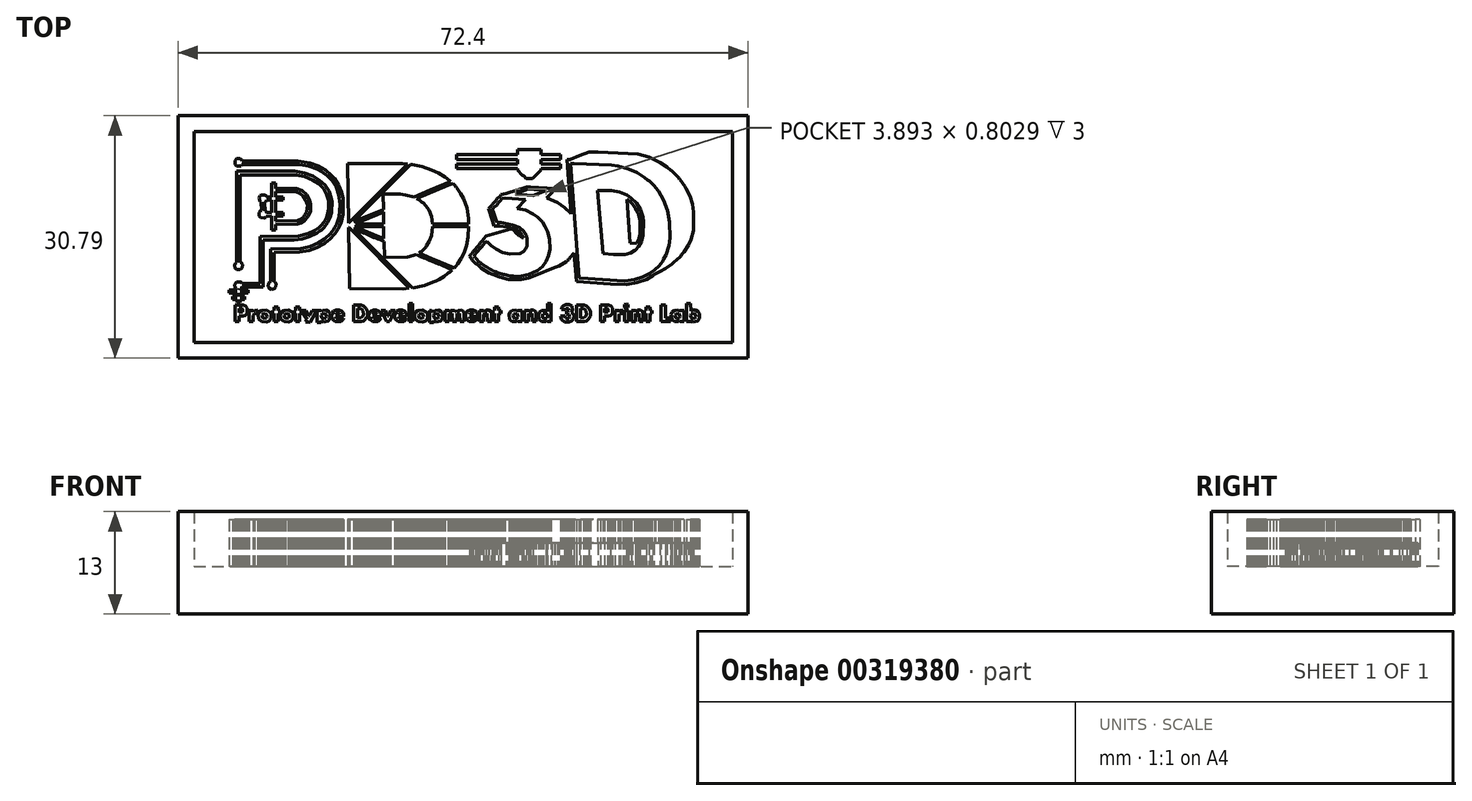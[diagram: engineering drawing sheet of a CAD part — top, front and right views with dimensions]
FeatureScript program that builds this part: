
annotation { "Feature Type Name" : "Feature", "Feature Type Description" : "" }
export const myFeature = defineFeature(function(context is Context, id is Id, definition is map)
    precondition{}
    {
        {
            var Q0;
            Q0=qCreatedBy(makeId("Top.planeOp"),FACE);
            var sketch = newSketch(context, id + "F0", { "sketchPlane" : qUnion([Q0])});
            skLineSegment(sketch, "E0", {"start": v(0.17, -1.62) * mm, "end": v(0.12, -1.63) * mm});
            skLineSegment(sketch, "E1", {"start": v(0.12, -1.63) * mm, "end": v(0.1, -1.66) * mm});
            skLineSegment(sketch, "E2", {"start": v(0.1, -1.66) * mm, "end": v(0.2, -1.65) * mm});
            skLineSegment(sketch, "E3", {"start": v(0.2, -1.65) * mm, "end": v(0.19, -1.63) * mm});
            skLineSegment(sketch, "E4", {"start": v(0.19, -1.63) * mm, "end": v(0.17, -1.62) * mm});
            skLineSegment(sketch, "E5", {"start": v(-1.33, -1.62) * mm, "end": v(-1.38, -1.63) * mm});
            skLineSegment(sketch, "E6", {"start": v(-1.38, -1.63) * mm, "end": v(-1.4, -1.66) * mm});
            skLineSegment(sketch, "E7", {"start": v(-1.4, -1.66) * mm, "end": v(-1.3, -1.65) * mm});
            skLineSegment(sketch, "E8", {"start": v(-1.3, -1.65) * mm, "end": v(-1.31, -1.63) * mm});
            skLineSegment(sketch, "E9", {"start": v(-1.31, -1.63) * mm, "end": v(-1.33, -1.62) * mm});
            skLineSegment(sketch, "E10", {"start": v(-1.87, -1.62) * mm, "end": v(-1.92, -1.63) * mm});
            skLineSegment(sketch, "E11", {"start": v(-1.92, -1.63) * mm, "end": v(-1.94, -1.66) * mm});
            skLineSegment(sketch, "E12", {"start": v(-1.94, -1.66) * mm, "end": v(-1.85, -1.65) * mm});
            skLineSegment(sketch, "E13", {"start": v(-1.85, -1.65) * mm, "end": v(-1.86, -1.63) * mm});
            skLineSegment(sketch, "E14", {"start": v(-1.86, -1.63) * mm, "end": v(-1.87, -1.62) * mm});
            skLineSegment(sketch, "E15", {"start": v(-2.66, -1.62) * mm, "end": v(-2.71, -1.63) * mm});
            skLineSegment(sketch, "E16", {"start": v(-2.71, -1.63) * mm, "end": v(-2.73, -1.66) * mm});
            skLineSegment(sketch, "E17", {"start": v(-2.73, -1.66) * mm, "end": v(-2.64, -1.65) * mm});
            skLineSegment(sketch, "E18", {"start": v(-2.64, -1.65) * mm, "end": v(-2.64, -1.63) * mm});
            skLineSegment(sketch, "E19", {"start": v(-2.64, -1.63) * mm, "end": v(-2.66, -1.62) * mm});
            skLineSegment(sketch, "E20", {"start": v(4.87, -1.64) * mm, "end": v(4.8, -1.65) * mm});
            skLineSegment(sketch, "E21", {"start": v(4.8, -1.65) * mm, "end": v(4.79, -1.67) * mm});
            skLineSegment(sketch, "E22", {"start": v(4.79, -1.67) * mm, "end": v(4.8, -1.72) * mm});
            skLineSegment(sketch, "E23", {"start": v(4.8, -1.72) * mm, "end": v(4.8, -1.72) * mm});
            skLineSegment(sketch, "E24", {"start": v(4.8, -1.72) * mm, "end": v(4.82, -1.74) * mm});
            skLineSegment(sketch, "E25", {"start": v(4.82, -1.74) * mm, "end": v(4.89, -1.73) * mm});
            skLineSegment(sketch, "E26", {"start": v(4.89, -1.73) * mm, "end": v(4.9, -1.7) * mm});
            skLineSegment(sketch, "E27", {"start": v(4.9, -1.7) * mm, "end": v(4.9, -1.66) * mm});
            skLineSegment(sketch, "E28", {"start": v(4.9, -1.66) * mm, "end": v(4.87, -1.64) * mm});
            skLineSegment(sketch, "E29", {"start": v(4.55, -1.64) * mm, "end": v(4.48, -1.65) * mm});
            skLineSegment(sketch, "E30", {"start": v(4.48, -1.65) * mm, "end": v(4.46, -1.67) * mm});
            skLineSegment(sketch, "E31", {"start": v(4.46, -1.67) * mm, "end": v(4.47, -1.72) * mm});
            skLineSegment(sketch, "E32", {"start": v(4.47, -1.72) * mm, "end": v(4.48, -1.72) * mm});
            skLineSegment(sketch, "E33", {"start": v(4.48, -1.72) * mm, "end": v(4.5, -1.74) * mm});
            skLineSegment(sketch, "E34", {"start": v(4.5, -1.74) * mm, "end": v(4.55, -1.73) * mm});
            skLineSegment(sketch, "E35", {"start": v(4.55, -1.73) * mm, "end": v(4.57, -1.72) * mm});
            skLineSegment(sketch, "E36", {"start": v(4.57, -1.72) * mm, "end": v(4.56, -1.66) * mm});
            skLineSegment(sketch, "E37", {"start": v(4.56, -1.66) * mm, "end": v(4.55, -1.64) * mm});
            skLineSegment(sketch, "E38", {"start": v(1.73, -1.64) * mm, "end": v(1.67, -1.65) * mm});
            skLineSegment(sketch, "E39", {"start": v(1.67, -1.65) * mm, "end": v(1.65, -1.67) * mm});
            skLineSegment(sketch, "E40", {"start": v(1.65, -1.67) * mm, "end": v(1.66, -1.72) * mm});
            skLineSegment(sketch, "E41", {"start": v(1.66, -1.72) * mm, "end": v(1.67, -1.72) * mm});
            skLineSegment(sketch, "E42", {"start": v(1.67, -1.72) * mm, "end": v(1.68, -1.74) * mm});
            skLineSegment(sketch, "E43", {"start": v(1.68, -1.74) * mm, "end": v(1.75, -1.73) * mm});
            skLineSegment(sketch, "E44", {"start": v(1.75, -1.73) * mm, "end": v(1.77, -1.7) * mm});
            skLineSegment(sketch, "E45", {"start": v(1.77, -1.7) * mm, "end": v(1.76, -1.66) * mm});
            skLineSegment(sketch, "E46", {"start": v(1.76, -1.66) * mm, "end": v(1.73, -1.64) * mm});
            skLineSegment(sketch, "E47", {"start": v(1.11, -1.64) * mm, "end": v(1.05, -1.65) * mm});
            skLineSegment(sketch, "E48", {"start": v(1.05, -1.65) * mm, "end": v(1.03, -1.67) * mm});
            skLineSegment(sketch, "E49", {"start": v(1.03, -1.67) * mm, "end": v(1.04, -1.72) * mm});
            skLineSegment(sketch, "E50", {"start": v(1.04, -1.72) * mm, "end": v(1.05, -1.72) * mm});
            skLineSegment(sketch, "E51", {"start": v(1.05, -1.72) * mm, "end": v(1.06, -1.74) * mm});
            skLineSegment(sketch, "E52", {"start": v(1.06, -1.74) * mm, "end": v(1.12, -1.73) * mm});
            skLineSegment(sketch, "E53", {"start": v(1.12, -1.73) * mm, "end": v(1.14, -1.72) * mm});
            skLineSegment(sketch, "E54", {"start": v(1.14, -1.72) * mm, "end": v(1.13, -1.66) * mm});
            skLineSegment(sketch, "E55", {"start": v(1.13, -1.66) * mm, "end": v(1.11, -1.64) * mm});
            skLineSegment(sketch, "E56", {"start": v(-0.57, -1.64) * mm, "end": v(-0.64, -1.65) * mm});
            skLineSegment(sketch, "E57", {"start": v(-0.64, -1.65) * mm, "end": v(-0.65, -1.67) * mm});
            skLineSegment(sketch, "E58", {"start": v(-0.65, -1.67) * mm, "end": v(-0.64, -1.72) * mm});
            skLineSegment(sketch, "E59", {"start": v(-0.64, -1.72) * mm, "end": v(-0.64, -1.72) * mm});
            skLineSegment(sketch, "E60", {"start": v(-0.64, -1.72) * mm, "end": v(-0.62, -1.74) * mm});
            skLineSegment(sketch, "E61", {"start": v(-0.62, -1.74) * mm, "end": v(-0.55, -1.73) * mm});
            skLineSegment(sketch, "E62", {"start": v(-0.55, -1.73) * mm, "end": v(-0.54, -1.7) * mm});
            skLineSegment(sketch, "E63", {"start": v(-0.54, -1.7) * mm, "end": v(-0.55, -1.66) * mm});
            skLineSegment(sketch, "E64", {"start": v(-0.55, -1.66) * mm, "end": v(-0.57, -1.64) * mm});
            skLineSegment(sketch, "E65", {"start": v(-2.95, -1.64) * mm, "end": v(-3.02, -1.65) * mm});
            skLineSegment(sketch, "E66", {"start": v(-3.02, -1.65) * mm, "end": v(-3.03, -1.67) * mm});
            skLineSegment(sketch, "E67", {"start": v(-3.03, -1.67) * mm, "end": v(-3.02, -1.72) * mm});
            skLineSegment(sketch, "E68", {"start": v(-3.02, -1.72) * mm, "end": v(-3.02, -1.72) * mm});
            skLineSegment(sketch, "E69", {"start": v(-3.02, -1.72) * mm, "end": v(-3, -1.74) * mm});
            skLineSegment(sketch, "E70", {"start": v(-3, -1.74) * mm, "end": v(-2.93, -1.73) * mm});
            skLineSegment(sketch, "E71", {"start": v(-2.93, -1.73) * mm, "end": v(-2.92, -1.7) * mm});
            skLineSegment(sketch, "E72", {"start": v(-2.92, -1.7) * mm, "end": v(-2.92, -1.66) * mm});
            skLineSegment(sketch, "E73", {"start": v(-2.92, -1.66) * mm, "end": v(-2.95, -1.64) * mm});
            skLineSegment(sketch, "E74", {"start": v(-0.9, -1.64) * mm, "end": v(-0.95, -1.65) * mm});
            skLineSegment(sketch, "E75", {"start": v(-0.95, -1.65) * mm, "end": v(-0.97, -1.67) * mm});
            skLineSegment(sketch, "E76", {"start": v(-0.97, -1.67) * mm, "end": v(-0.96, -1.72) * mm});
            skLineSegment(sketch, "E77", {"start": v(-0.96, -1.72) * mm, "end": v(-0.95, -1.72) * mm});
            skLineSegment(sketch, "E78", {"start": v(-0.95, -1.72) * mm, "end": v(-0.95, -1.74) * mm});
            skLineSegment(sketch, "E79", {"start": v(-0.95, -1.74) * mm, "end": v(-0.88, -1.73) * mm});
            skLineSegment(sketch, "E80", {"start": v(-0.88, -1.73) * mm, "end": v(-0.86, -1.7) * mm});
            skLineSegment(sketch, "E81", {"start": v(-0.86, -1.7) * mm, "end": v(-0.87, -1.66) * mm});
            skLineSegment(sketch, "E82", {"start": v(-0.87, -1.66) * mm, "end": v(-0.9, -1.64) * mm});
            skLineSegment(sketch, "E83", {"start": v(-3.73, -1.64) * mm, "end": v(-3.8, -1.65) * mm});
            skLineSegment(sketch, "E84", {"start": v(-3.8, -1.65) * mm, "end": v(-3.81, -1.67) * mm});
            skLineSegment(sketch, "E85", {"start": v(-3.81, -1.67) * mm, "end": v(-3.8, -1.72) * mm});
            skLineSegment(sketch, "E86", {"start": v(-3.8, -1.72) * mm, "end": v(-3.8, -1.72) * mm});
            skLineSegment(sketch, "E87", {"start": v(-3.8, -1.72) * mm, "end": v(-3.79, -1.74) * mm});
            skLineSegment(sketch, "E88", {"start": v(-3.79, -1.74) * mm, "end": v(-3.72, -1.73) * mm});
            skLineSegment(sketch, "E89", {"start": v(-3.72, -1.73) * mm, "end": v(-3.7, -1.7) * mm});
            skLineSegment(sketch, "E90", {"start": v(-3.7, -1.7) * mm, "end": v(-3.71, -1.66) * mm});
            skLineSegment(sketch, "E91", {"start": v(-3.71, -1.66) * mm, "end": v(-3.73, -1.64) * mm});
            skLineSegment(sketch, "E92", {"start": v(-4.2, -1.64) * mm, "end": v(-4.27, -1.65) * mm});
            skLineSegment(sketch, "E93", {"start": v(-4.27, -1.65) * mm, "end": v(-4.28, -1.67) * mm});
            skLineSegment(sketch, "E94", {"start": v(-4.28, -1.67) * mm, "end": v(-4.27, -1.72) * mm});
            skLineSegment(sketch, "E95", {"start": v(-4.27, -1.72) * mm, "end": v(-4.27, -1.72) * mm});
            skLineSegment(sketch, "E96", {"start": v(-4.27, -1.72) * mm, "end": v(-4.26, -1.74) * mm});
            skLineSegment(sketch, "E97", {"start": v(-4.26, -1.74) * mm, "end": v(-4.19, -1.73) * mm});
            skLineSegment(sketch, "E98", {"start": v(-4.19, -1.73) * mm, "end": v(-4.17, -1.7) * mm});
            skLineSegment(sketch, "E99", {"start": v(-4.17, -1.7) * mm, "end": v(-4.18, -1.66) * mm});
            skLineSegment(sketch, "E100", {"start": v(-4.18, -1.66) * mm, "end": v(-4.2, -1.64) * mm});
            skLineSegment(sketch, "E101", {"start": v(3.45, -1.44) * mm, "end": v(3.47, -1.45) * mm});
            skLineSegment(sketch, "E102", {"start": v(3.47, -1.45) * mm, "end": v(3.47, -1.51) * mm});
            skLineSegment(sketch, "E103", {"start": v(3.47, -1.51) * mm, "end": v(3.42, -1.53) * mm});
            skLineSegment(sketch, "E104", {"start": v(3.42, -1.53) * mm, "end": v(3.4, -1.51) * mm});
            skLineSegment(sketch, "E105", {"start": v(3.4, -1.51) * mm, "end": v(3.4, -1.45) * mm});
            skLineSegment(sketch, "E106", {"start": v(3.4, -1.45) * mm, "end": v(3.45, -1.44) * mm});
            skLineSegment(sketch, "E107", {"start": v(2.21, -1.44) * mm, "end": v(2.28, -1.48) * mm});
            skLineSegment(sketch, "E108", {"start": v(2.28, -1.48) * mm, "end": v(2.3, -1.56) * mm});
            skLineSegment(sketch, "E109", {"start": v(2.3, -1.56) * mm, "end": v(2.27, -1.6) * mm});
            skLineSegment(sketch, "E110", {"start": v(2.27, -1.6) * mm, "end": v(2.26, -1.62) * mm});
            skLineSegment(sketch, "E111", {"start": v(2.26, -1.62) * mm, "end": v(2.28, -1.62) * mm});
            skLineSegment(sketch, "E112", {"start": v(2.28, -1.62) * mm, "end": v(2.32, -1.68) * mm});
            skLineSegment(sketch, "E113", {"start": v(2.32, -1.68) * mm, "end": v(2.31, -1.75) * mm});
            skLineSegment(sketch, "E114", {"start": v(2.31, -1.75) * mm, "end": v(2.27, -1.8) * mm});
            skLineSegment(sketch, "E115", {"start": v(2.27, -1.8) * mm, "end": v(2.21, -1.82) * mm});
            skLineSegment(sketch, "E116", {"start": v(2.21, -1.82) * mm, "end": v(2.12, -1.81) * mm});
            skLineSegment(sketch, "E117", {"start": v(2.12, -1.81) * mm, "end": v(2.06, -1.77) * mm});
            skLineSegment(sketch, "E118", {"start": v(2.06, -1.77) * mm, "end": v(2.04, -1.7) * mm});
            skLineSegment(sketch, "E119", {"start": v(2.04, -1.7) * mm, "end": v(2.13, -1.7) * mm});
            skLineSegment(sketch, "E120", {"start": v(2.13, -1.7) * mm, "end": v(2.14, -1.73) * mm});
            skLineSegment(sketch, "E121", {"start": v(2.14, -1.73) * mm, "end": v(2.15, -1.73) * mm});
            skLineSegment(sketch, "E122", {"start": v(2.15, -1.73) * mm, "end": v(2.16, -1.75) * mm});
            skLineSegment(sketch, "E123", {"start": v(2.16, -1.75) * mm, "end": v(2.21, -1.74) * mm});
            skLineSegment(sketch, "E124", {"start": v(2.21, -1.74) * mm, "end": v(2.23, -1.72) * mm});
            skLineSegment(sketch, "E125", {"start": v(2.23, -1.72) * mm, "end": v(2.22, -1.66) * mm});
            skLineSegment(sketch, "E126", {"start": v(2.22, -1.66) * mm, "end": v(2.17, -1.65) * mm});
            skLineSegment(sketch, "E127", {"start": v(2.17, -1.65) * mm, "end": v(2.17, -1.59) * mm});
            skLineSegment(sketch, "E128", {"start": v(2.17, -1.59) * mm, "end": v(2.21, -1.57) * mm});
            skLineSegment(sketch, "E129", {"start": v(2.21, -1.57) * mm, "end": v(2.2, -1.53) * mm});
            skLineSegment(sketch, "E130", {"start": v(2.2, -1.53) * mm, "end": v(2.15, -1.53) * mm});
            skLineSegment(sketch, "E131", {"start": v(2.15, -1.53) * mm, "end": v(2.14, -1.56) * mm});
            skLineSegment(sketch, "E132", {"start": v(2.14, -1.56) * mm, "end": v(2.06, -1.55) * mm});
            skLineSegment(sketch, "E133", {"start": v(2.06, -1.55) * mm, "end": v(2.07, -1.5) * mm});
            skLineSegment(sketch, "E134", {"start": v(2.07, -1.5) * mm, "end": v(2.1, -1.47) * mm});
            skLineSegment(sketch, "E135", {"start": v(2.1, -1.47) * mm, "end": v(2.15, -1.44) * mm});
            skLineSegment(sketch, "E136", {"start": v(2.15, -1.44) * mm, "end": v(2.21, -1.44) * mm});
            skLineSegment(sketch, "E137", {"start": v(3.05, -1.46) * mm, "end": v(3.1, -1.48) * mm});
            skLineSegment(sketch, "E138", {"start": v(3.1, -1.48) * mm, "end": v(3.14, -1.52) * mm});
            skLineSegment(sketch, "E139", {"start": v(3.14, -1.52) * mm, "end": v(3.14, -1.63) * mm});
            skLineSegment(sketch, "E140", {"start": v(3.14, -1.63) * mm, "end": v(3.1, -1.68) * mm});
            skLineSegment(sketch, "E141", {"start": v(3.1, -1.68) * mm, "end": v(3.05, -1.7) * mm});
            skLineSegment(sketch, "E142", {"start": v(3.05, -1.7) * mm, "end": v(2.97, -1.7) * mm});
            skLineSegment(sketch, "E143", {"start": v(2.97, -1.7) * mm, "end": v(2.97, -1.8) * mm});
            skLineSegment(sketch, "E144", {"start": v(2.97, -1.8) * mm, "end": v(2.88, -1.8) * mm});
            skLineSegment(sketch, "E145", {"start": v(2.88, -1.8) * mm, "end": v(2.88, -1.46) * mm});
            skLineSegment(sketch, "E146", {"start": v(2.88, -1.46) * mm, "end": v(3.05, -1.46) * mm});
            skLineSegment(sketch, "E147", {"start": v(2.54, -1.46) * mm, "end": v(2.6, -1.48) * mm});
            skLineSegment(sketch, "E148", {"start": v(2.6, -1.48) * mm, "end": v(2.64, -1.53) * mm});
            skLineSegment(sketch, "E149", {"start": v(2.64, -1.53) * mm, "end": v(2.67, -1.6) * mm});
            skLineSegment(sketch, "E150", {"start": v(2.67, -1.6) * mm, "end": v(2.67, -1.7) * mm});
            skLineSegment(sketch, "E151", {"start": v(2.67, -1.7) * mm, "end": v(2.63, -1.75) * mm});
            skLineSegment(sketch, "E152", {"start": v(2.63, -1.75) * mm, "end": v(2.58, -1.8) * mm});
            skLineSegment(sketch, "E153", {"start": v(2.58, -1.8) * mm, "end": v(2.54, -1.8) * mm});
            skLineSegment(sketch, "E154", {"start": v(2.54, -1.8) * mm, "end": v(2.37, -1.8) * mm});
            skLineSegment(sketch, "E155", {"start": v(2.37, -1.8) * mm, "end": v(2.37, -1.46) * mm});
            skLineSegment(sketch, "E156", {"start": v(2.37, -1.46) * mm, "end": v(2.54, -1.46) * mm});
            skLineSegment(sketch, "E157", {"start": v(-2.18, -1.46) * mm, "end": v(-2.13, -1.48) * mm});
            skLineSegment(sketch, "E158", {"start": v(-2.13, -1.48) * mm, "end": v(-2.08, -1.53) * mm});
            skLineSegment(sketch, "E159", {"start": v(-2.08, -1.53) * mm, "end": v(-2.05, -1.6) * mm});
            skLineSegment(sketch, "E160", {"start": v(-2.05, -1.6) * mm, "end": v(-2.05, -1.7) * mm});
            skLineSegment(sketch, "E161", {"start": v(-2.05, -1.7) * mm, "end": v(-2.1, -1.76) * mm});
            skLineSegment(sketch, "E162", {"start": v(-2.1, -1.76) * mm, "end": v(-2.14, -1.8) * mm});
            skLineSegment(sketch, "E163", {"start": v(-2.14, -1.8) * mm, "end": v(-2.18, -1.8) * mm});
            skLineSegment(sketch, "E164", {"start": v(-2.18, -1.8) * mm, "end": v(-2.35, -1.8) * mm});
            skLineSegment(sketch, "E165", {"start": v(-2.35, -1.8) * mm, "end": v(-2.35, -1.46) * mm});
            skLineSegment(sketch, "E166", {"start": v(-2.35, -1.46) * mm, "end": v(-2.18, -1.46) * mm});
            skLineSegment(sketch, "E167", {"start": v(-4.68, -1.46) * mm, "end": v(-4.63, -1.48) * mm});
            skLineSegment(sketch, "E168", {"start": v(-4.63, -1.48) * mm, "end": v(-4.6, -1.52) * mm});
            skLineSegment(sketch, "E169", {"start": v(-4.6, -1.52) * mm, "end": v(-4.6, -1.63) * mm});
            skLineSegment(sketch, "E170", {"start": v(-4.6, -1.63) * mm, "end": v(-4.64, -1.68) * mm});
            skLineSegment(sketch, "E171", {"start": v(-4.64, -1.68) * mm, "end": v(-4.68, -1.7) * mm});
            skLineSegment(sketch, "E172", {"start": v(-4.68, -1.7) * mm, "end": v(-4.77, -1.7) * mm});
            skLineSegment(sketch, "E173", {"start": v(-4.77, -1.7) * mm, "end": v(-4.77, -1.8) * mm});
            skLineSegment(sketch, "E174", {"start": v(-4.77, -1.8) * mm, "end": v(-4.86, -1.8) * mm});
            skLineSegment(sketch, "E175", {"start": v(-4.86, -1.8) * mm, "end": v(-4.86, -1.46) * mm});
            skLineSegment(sketch, "E176", {"start": v(-4.86, -1.46) * mm, "end": v(-4.68, -1.46) * mm});
            skLineSegment(sketch, "E177", {"start": v(4.52, -1.56) * mm, "end": v(4.57, -1.6) * mm});
            skLineSegment(sketch, "E178", {"start": v(4.57, -1.6) * mm, "end": v(4.57, -1.57) * mm});
            skLineSegment(sketch, "E179", {"start": v(4.57, -1.57) * mm, "end": v(4.65, -1.57) * mm});
            skLineSegment(sketch, "E180", {"start": v(4.65, -1.57) * mm, "end": v(4.65, -1.8) * mm});
            skLineSegment(sketch, "E181", {"start": v(4.65, -1.8) * mm, "end": v(4.57, -1.8) * mm});
            skLineSegment(sketch, "E182", {"start": v(4.57, -1.8) * mm, "end": v(4.56, -1.78) * mm});
            skLineSegment(sketch, "E183", {"start": v(4.56, -1.78) * mm, "end": v(4.54, -1.8) * mm});
            skLineSegment(sketch, "E184", {"start": v(4.54, -1.8) * mm, "end": v(4.45, -1.8) * mm});
            skLineSegment(sketch, "E185", {"start": v(4.45, -1.8) * mm, "end": v(4.4, -1.76) * mm});
            skLineSegment(sketch, "E186", {"start": v(4.4, -1.76) * mm, "end": v(4.38, -1.66) * mm});
            skLineSegment(sketch, "E187", {"start": v(4.38, -1.66) * mm, "end": v(4.4, -1.6) * mm});
            skLineSegment(sketch, "E188", {"start": v(4.4, -1.6) * mm, "end": v(4.45, -1.57) * mm});
            skLineSegment(sketch, "E189", {"start": v(4.45, -1.57) * mm, "end": v(4.52, -1.56) * mm});
            skLineSegment(sketch, "E190", {"start": v(3.93, -1.5) * mm, "end": v(3.93, -1.57) * mm});
            skLineSegment(sketch, "E191", {"start": v(3.93, -1.57) * mm, "end": v(3.98, -1.57) * mm});
            skLineSegment(sketch, "E192", {"start": v(3.98, -1.57) * mm, "end": v(3.98, -1.64) * mm});
            skLineSegment(sketch, "E193", {"start": v(3.98, -1.64) * mm, "end": v(3.93, -1.64) * mm});
            skLineSegment(sketch, "E194", {"start": v(3.93, -1.64) * mm, "end": v(3.93, -1.8) * mm});
            skLineSegment(sketch, "E195", {"start": v(3.93, -1.8) * mm, "end": v(3.85, -1.8) * mm});
            skLineSegment(sketch, "E196", {"start": v(3.85, -1.8) * mm, "end": v(3.85, -1.64) * mm});
            skLineSegment(sketch, "E197", {"start": v(3.85, -1.64) * mm, "end": v(3.82, -1.64) * mm});
            skLineSegment(sketch, "E198", {"start": v(3.82, -1.64) * mm, "end": v(3.82, -1.57) * mm});
            skLineSegment(sketch, "E199", {"start": v(3.82, -1.57) * mm, "end": v(3.85, -1.57) * mm});
            skLineSegment(sketch, "E200", {"start": v(3.85, -1.57) * mm, "end": v(3.85, -1.5) * mm});
            skLineSegment(sketch, "E201", {"start": v(3.85, -1.5) * mm, "end": v(3.93, -1.5) * mm});
            skLineSegment(sketch, "E202", {"start": v(3.73, -1.56) * mm, "end": v(3.77, -1.6) * mm});
            skLineSegment(sketch, "E203", {"start": v(3.77, -1.6) * mm, "end": v(3.79, -1.63) * mm});
            skLineSegment(sketch, "E204", {"start": v(3.79, -1.63) * mm, "end": v(3.79, -1.8) * mm});
            skLineSegment(sketch, "E205", {"start": v(3.79, -1.8) * mm, "end": v(3.7, -1.8) * mm});
            skLineSegment(sketch, "E206", {"start": v(3.7, -1.8) * mm, "end": v(3.7, -1.64) * mm});
            skLineSegment(sketch, "E207", {"start": v(3.7, -1.64) * mm, "end": v(3.64, -1.64) * mm});
            skLineSegment(sketch, "E208", {"start": v(3.64, -1.64) * mm, "end": v(3.62, -1.66) * mm});
            skLineSegment(sketch, "E209", {"start": v(3.62, -1.66) * mm, "end": v(3.62, -1.8) * mm});
            skLineSegment(sketch, "E210", {"start": v(3.62, -1.8) * mm, "end": v(3.54, -1.8) * mm});
            skLineSegment(sketch, "E211", {"start": v(3.54, -1.8) * mm, "end": v(3.54, -1.57) * mm});
            skLineSegment(sketch, "E212", {"start": v(3.54, -1.57) * mm, "end": v(3.62, -1.57) * mm});
            skLineSegment(sketch, "E213", {"start": v(3.62, -1.57) * mm, "end": v(3.63, -1.6) * mm});
            skLineSegment(sketch, "E214", {"start": v(3.63, -1.6) * mm, "end": v(3.64, -1.58) * mm});
            skLineSegment(sketch, "E215", {"start": v(3.64, -1.58) * mm, "end": v(3.67, -1.56) * mm});
            skLineSegment(sketch, "E216", {"start": v(3.67, -1.56) * mm, "end": v(3.73, -1.56) * mm});
            skLineSegment(sketch, "E217", {"start": v(1.46, -1.56) * mm, "end": v(1.5, -1.6) * mm});
            skLineSegment(sketch, "E218", {"start": v(1.5, -1.6) * mm, "end": v(1.52, -1.63) * mm});
            skLineSegment(sketch, "E219", {"start": v(1.52, -1.63) * mm, "end": v(1.52, -1.8) * mm});
            skLineSegment(sketch, "E220", {"start": v(1.52, -1.8) * mm, "end": v(1.44, -1.8) * mm});
            skLineSegment(sketch, "E221", {"start": v(1.44, -1.8) * mm, "end": v(1.43, -1.64) * mm});
            skLineSegment(sketch, "E222", {"start": v(1.43, -1.64) * mm, "end": v(1.37, -1.64) * mm});
            skLineSegment(sketch, "E223", {"start": v(1.37, -1.64) * mm, "end": v(1.36, -1.66) * mm});
            skLineSegment(sketch, "E224", {"start": v(1.36, -1.66) * mm, "end": v(1.36, -1.8) * mm});
            skLineSegment(sketch, "E225", {"start": v(1.36, -1.8) * mm, "end": v(1.27, -1.8) * mm});
            skLineSegment(sketch, "E226", {"start": v(1.27, -1.8) * mm, "end": v(1.27, -1.57) * mm});
            skLineSegment(sketch, "E227", {"start": v(1.27, -1.57) * mm, "end": v(1.36, -1.57) * mm});
            skLineSegment(sketch, "E228", {"start": v(1.36, -1.57) * mm, "end": v(1.36, -1.6) * mm});
            skLineSegment(sketch, "E229", {"start": v(1.36, -1.6) * mm, "end": v(1.37, -1.58) * mm});
            skLineSegment(sketch, "E230", {"start": v(1.37, -1.58) * mm, "end": v(1.4, -1.56) * mm});
            skLineSegment(sketch, "E231", {"start": v(1.4, -1.56) * mm, "end": v(1.46, -1.56) * mm});
            skLineSegment(sketch, "E232", {"start": v(1.1, -1.56) * mm, "end": v(1.14, -1.6) * mm});
            skLineSegment(sketch, "E233", {"start": v(1.14, -1.6) * mm, "end": v(1.14, -1.57) * mm});
            skLineSegment(sketch, "E234", {"start": v(1.14, -1.57) * mm, "end": v(1.22, -1.57) * mm});
            skLineSegment(sketch, "E235", {"start": v(1.22, -1.57) * mm, "end": v(1.22, -1.8) * mm});
            skLineSegment(sketch, "E236", {"start": v(1.22, -1.8) * mm, "end": v(1.14, -1.8) * mm});
            skLineSegment(sketch, "E237", {"start": v(1.14, -1.8) * mm, "end": v(1.13, -1.78) * mm});
            skLineSegment(sketch, "E238", {"start": v(1.13, -1.78) * mm, "end": v(1.1, -1.8) * mm});
            skLineSegment(sketch, "E239", {"start": v(1.1, -1.8) * mm, "end": v(1.02, -1.8) * mm});
            skLineSegment(sketch, "E240", {"start": v(1.02, -1.8) * mm, "end": v(0.96, -1.76) * mm});
            skLineSegment(sketch, "E241", {"start": v(0.96, -1.76) * mm, "end": v(0.95, -1.66) * mm});
            skLineSegment(sketch, "E242", {"start": v(0.95, -1.66) * mm, "end": v(0.97, -1.6) * mm});
            skLineSegment(sketch, "E243", {"start": v(0.97, -1.6) * mm, "end": v(1.02, -1.57) * mm});
            skLineSegment(sketch, "E244", {"start": v(1.02, -1.57) * mm, "end": v(1.1, -1.56) * mm});
            skLineSegment(sketch, "E245", {"start": v(0.73, -1.5) * mm, "end": v(0.73, -1.57) * mm});
            skLineSegment(sketch, "E246", {"start": v(0.73, -1.57) * mm, "end": v(0.77, -1.57) * mm});
            skLineSegment(sketch, "E247", {"start": v(0.77, -1.57) * mm, "end": v(0.77, -1.64) * mm});
            skLineSegment(sketch, "E248", {"start": v(0.77, -1.64) * mm, "end": v(0.73, -1.64) * mm});
            skLineSegment(sketch, "E249", {"start": v(0.73, -1.64) * mm, "end": v(0.73, -1.8) * mm});
            skLineSegment(sketch, "E250", {"start": v(0.73, -1.8) * mm, "end": v(0.64, -1.8) * mm});
            skLineSegment(sketch, "E251", {"start": v(0.64, -1.8) * mm, "end": v(0.64, -1.64) * mm});
            skLineSegment(sketch, "E252", {"start": v(0.64, -1.64) * mm, "end": v(0.61, -1.64) * mm});
            skLineSegment(sketch, "E253", {"start": v(0.61, -1.64) * mm, "end": v(0.61, -1.57) * mm});
            skLineSegment(sketch, "E254", {"start": v(0.61, -1.57) * mm, "end": v(0.64, -1.57) * mm});
            skLineSegment(sketch, "E255", {"start": v(0.64, -1.57) * mm, "end": v(0.64, -1.5) * mm});
            skLineSegment(sketch, "E256", {"start": v(0.64, -1.5) * mm, "end": v(0.73, -1.5) * mm});
            skLineSegment(sketch, "E257", {"start": v(0.52, -1.56) * mm, "end": v(0.56, -1.6) * mm});
            skLineSegment(sketch, "E258", {"start": v(0.56, -1.6) * mm, "end": v(0.58, -1.63) * mm});
            skLineSegment(sketch, "E259", {"start": v(0.58, -1.63) * mm, "end": v(0.58, -1.8) * mm});
            skLineSegment(sketch, "E260", {"start": v(0.58, -1.8) * mm, "end": v(0.5, -1.8) * mm});
            skLineSegment(sketch, "E261", {"start": v(0.5, -1.8) * mm, "end": v(0.48, -1.64) * mm});
            skLineSegment(sketch, "E262", {"start": v(0.48, -1.64) * mm, "end": v(0.42, -1.64) * mm});
            skLineSegment(sketch, "E263", {"start": v(0.42, -1.64) * mm, "end": v(0.4, -1.66) * mm});
            skLineSegment(sketch, "E264", {"start": v(0.4, -1.66) * mm, "end": v(0.4, -1.8) * mm});
            skLineSegment(sketch, "E265", {"start": v(0.4, -1.8) * mm, "end": v(0.33, -1.8) * mm});
            skLineSegment(sketch, "E266", {"start": v(0.33, -1.8) * mm, "end": v(0.33, -1.57) * mm});
            skLineSegment(sketch, "E267", {"start": v(0.33, -1.57) * mm, "end": v(0.4, -1.57) * mm});
            skLineSegment(sketch, "E268", {"start": v(0.4, -1.57) * mm, "end": v(0.42, -1.6) * mm});
            skLineSegment(sketch, "E269", {"start": v(0.42, -1.6) * mm, "end": v(0.42, -1.58) * mm});
            skLineSegment(sketch, "E270", {"start": v(0.42, -1.58) * mm, "end": v(0.45, -1.56) * mm});
            skLineSegment(sketch, "E271", {"start": v(0.45, -1.56) * mm, "end": v(0.52, -1.56) * mm});
            skLineSegment(sketch, "E272", {"start": v(0.18, -1.56) * mm, "end": v(0.23, -1.59) * mm});
            skLineSegment(sketch, "E273", {"start": v(0.23, -1.59) * mm, "end": v(0.26, -1.6) * mm});
            skLineSegment(sketch, "E274", {"start": v(0.26, -1.6) * mm, "end": v(0.28, -1.65) * mm});
            skLineSegment(sketch, "E275", {"start": v(0.28, -1.65) * mm, "end": v(0.28, -1.7) * mm});
            skLineSegment(sketch, "E276", {"start": v(0.28, -1.7) * mm, "end": v(0.1, -1.7) * mm});
            skLineSegment(sketch, "E277", {"start": v(0.1, -1.7) * mm, "end": v(0.12, -1.75) * mm});
            skLineSegment(sketch, "E278", {"start": v(0.12, -1.75) * mm, "end": v(0.14, -1.75) * mm});
            skLineSegment(sketch, "E279", {"start": v(0.14, -1.75) * mm, "end": v(0.18, -1.75) * mm});
            skLineSegment(sketch, "E280", {"start": v(0.18, -1.75) * mm, "end": v(0.2, -1.73) * mm});
            skLineSegment(sketch, "E281", {"start": v(0.2, -1.73) * mm, "end": v(0.28, -1.73) * mm});
            skLineSegment(sketch, "E282", {"start": v(0.28, -1.73) * mm, "end": v(0.27, -1.77) * mm});
            skLineSegment(sketch, "E283", {"start": v(0.27, -1.77) * mm, "end": v(0.22, -1.8) * mm});
            skLineSegment(sketch, "E284", {"start": v(0.22, -1.8) * mm, "end": v(0.1, -1.8) * mm});
            skLineSegment(sketch, "E285", {"start": v(0.1, -1.8) * mm, "end": v(0.05, -1.77) * mm});
            skLineSegment(sketch, "E286", {"start": v(0.05, -1.77) * mm, "end": v(0.02, -1.72) * mm});
            skLineSegment(sketch, "E287", {"start": v(0.02, -1.72) * mm, "end": v(0.03, -1.63) * mm});
            skLineSegment(sketch, "E288", {"start": v(0.03, -1.63) * mm, "end": v(0.07, -1.59) * mm});
            skLineSegment(sketch, "E289", {"start": v(0.07, -1.59) * mm, "end": v(0.12, -1.56) * mm});
            skLineSegment(sketch, "E290", {"start": v(0.12, -1.56) * mm, "end": v(0.18, -1.56) * mm});
            skLineSegment(sketch, "E291", {"start": v(-0.06, -1.56) * mm, "end": v(-0.02, -1.59) * mm});
            skLineSegment(sketch, "E292", {"start": v(-0.02, -1.59) * mm, "end": v(0, -1.63) * mm});
            skLineSegment(sketch, "E293", {"start": v(0, -1.63) * mm, "end": v(0, -1.8) * mm});
            skLineSegment(sketch, "E294", {"start": v(0, -1.8) * mm, "end": v(-0.1, -1.8) * mm});
            skLineSegment(sketch, "E295", {"start": v(-0.1, -1.8) * mm, "end": v(-0.1, -1.64) * mm});
            skLineSegment(sketch, "E296", {"start": v(-0.1, -1.64) * mm, "end": v(-0.16, -1.64) * mm});
            skLineSegment(sketch, "E297", {"start": v(-0.16, -1.64) * mm, "end": v(-0.17, -1.8) * mm});
            skLineSegment(sketch, "E298", {"start": v(-0.17, -1.8) * mm, "end": v(-0.25, -1.8) * mm});
            skLineSegment(sketch, "E299", {"start": v(-0.25, -1.8) * mm, "end": v(-0.26, -1.64) * mm});
            skLineSegment(sketch, "E300", {"start": v(-0.26, -1.64) * mm, "end": v(-0.32, -1.64) * mm});
            skLineSegment(sketch, "E301", {"start": v(-0.32, -1.64) * mm, "end": v(-0.33, -1.8) * mm});
            skLineSegment(sketch, "E302", {"start": v(-0.33, -1.8) * mm, "end": v(-0.4, -1.8) * mm});
            skLineSegment(sketch, "E303", {"start": v(-0.4, -1.8) * mm, "end": v(-0.4, -1.57) * mm});
            skLineSegment(sketch, "E304", {"start": v(-0.4, -1.57) * mm, "end": v(-0.33, -1.57) * mm});
            skLineSegment(sketch, "E305", {"start": v(-0.33, -1.57) * mm, "end": v(-0.32, -1.6) * mm});
            skLineSegment(sketch, "E306", {"start": v(-0.32, -1.6) * mm, "end": v(-0.3, -1.57) * mm});
            skLineSegment(sketch, "E307", {"start": v(-0.3, -1.57) * mm, "end": v(-0.2, -1.57) * mm});
            skLineSegment(sketch, "E308", {"start": v(-0.2, -1.57) * mm, "end": v(-0.17, -1.6) * mm});
            skLineSegment(sketch, "E309", {"start": v(-0.17, -1.6) * mm, "end": v(-0.17, -1.6) * mm});
            skLineSegment(sketch, "E310", {"start": v(-0.17, -1.6) * mm, "end": v(-0.14, -1.57) * mm});
            skLineSegment(sketch, "E311", {"start": v(-0.14, -1.57) * mm, "end": v(-0.06, -1.56) * mm});
            skLineSegment(sketch, "E312", {"start": v(-0.55, -1.56) * mm, "end": v(-0.5, -1.6) * mm});
            skLineSegment(sketch, "E313", {"start": v(-0.5, -1.6) * mm, "end": v(-0.46, -1.64) * mm});
            skLineSegment(sketch, "E314", {"start": v(-0.46, -1.64) * mm, "end": v(-0.46, -1.75) * mm});
            skLineSegment(sketch, "E315", {"start": v(-0.46, -1.75) * mm, "end": v(-0.5, -1.8) * mm});
            skLineSegment(sketch, "E316", {"start": v(-0.5, -1.8) * mm, "end": v(-0.6, -1.81) * mm});
            skLineSegment(sketch, "E317", {"start": v(-0.6, -1.81) * mm, "end": v(-0.65, -1.78) * mm});
            skLineSegment(sketch, "E318", {"start": v(-0.65, -1.78) * mm, "end": v(-0.65, -1.83) * mm});
            skLineSegment(sketch, "E319", {"start": v(-0.65, -1.83) * mm, "end": v(-0.73, -1.83) * mm});
            skLineSegment(sketch, "E320", {"start": v(-0.73, -1.83) * mm, "end": v(-0.73, -1.57) * mm});
            skLineSegment(sketch, "E321", {"start": v(-0.73, -1.57) * mm, "end": v(-0.69, -1.57) * mm});
            skLineSegment(sketch, "E322", {"start": v(-0.69, -1.57) * mm, "end": v(-0.67, -1.6) * mm});
            skLineSegment(sketch, "E323", {"start": v(-0.67, -1.6) * mm, "end": v(-0.64, -1.6) * mm});
            skLineSegment(sketch, "E324", {"start": v(-0.64, -1.6) * mm, "end": v(-0.62, -1.57) * mm});
            skLineSegment(sketch, "E325", {"start": v(-0.62, -1.57) * mm, "end": v(-0.55, -1.56) * mm});
            skLineSegment(sketch, "E326", {"start": v(-0.88, -1.56) * mm, "end": v(-0.81, -1.6) * mm});
            skLineSegment(sketch, "E327", {"start": v(-0.81, -1.6) * mm, "end": v(-0.78, -1.64) * mm});
            skLineSegment(sketch, "E328", {"start": v(-0.78, -1.64) * mm, "end": v(-0.78, -1.74) * mm});
            skLineSegment(sketch, "E329", {"start": v(-0.78, -1.74) * mm, "end": v(-0.83, -1.8) * mm});
            skLineSegment(sketch, "E330", {"start": v(-0.83, -1.8) * mm, "end": v(-0.88, -1.81) * mm});
            skLineSegment(sketch, "E331", {"start": v(-0.88, -1.81) * mm, "end": v(-0.98, -1.8) * mm});
            skLineSegment(sketch, "E332", {"start": v(-0.98, -1.8) * mm, "end": v(-1.05, -1.75) * mm});
            skLineSegment(sketch, "E333", {"start": v(-1.05, -1.75) * mm, "end": v(-1.06, -1.66) * mm});
            skLineSegment(sketch, "E334", {"start": v(-1.06, -1.66) * mm, "end": v(-1.03, -1.6) * mm});
            skLineSegment(sketch, "E335", {"start": v(-1.03, -1.6) * mm, "end": v(-0.98, -1.57) * mm});
            skLineSegment(sketch, "E336", {"start": v(-0.98, -1.57) * mm, "end": v(-0.88, -1.56) * mm});
            skLineSegment(sketch, "E337", {"start": v(-1.32, -1.56) * mm, "end": v(-1.27, -1.59) * mm});
            skLineSegment(sketch, "E338", {"start": v(-1.27, -1.59) * mm, "end": v(-1.23, -1.62) * mm});
            skLineSegment(sketch, "E339", {"start": v(-1.23, -1.62) * mm, "end": v(-1.22, -1.65) * mm});
            skLineSegment(sketch, "E340", {"start": v(-1.22, -1.65) * mm, "end": v(-1.22, -1.7) * mm});
            skLineSegment(sketch, "E341", {"start": v(-1.22, -1.7) * mm, "end": v(-1.4, -1.7) * mm});
            skLineSegment(sketch, "E342", {"start": v(-1.4, -1.7) * mm, "end": v(-1.38, -1.75) * mm});
            skLineSegment(sketch, "E343", {"start": v(-1.38, -1.75) * mm, "end": v(-1.36, -1.75) * mm});
            skLineSegment(sketch, "E344", {"start": v(-1.36, -1.75) * mm, "end": v(-1.32, -1.75) * mm});
            skLineSegment(sketch, "E345", {"start": v(-1.32, -1.75) * mm, "end": v(-1.3, -1.73) * mm});
            skLineSegment(sketch, "E346", {"start": v(-1.3, -1.73) * mm, "end": v(-1.22, -1.73) * mm});
            skLineSegment(sketch, "E347", {"start": v(-1.22, -1.73) * mm, "end": v(-1.23, -1.77) * mm});
            skLineSegment(sketch, "E348", {"start": v(-1.23, -1.77) * mm, "end": v(-1.28, -1.8) * mm});
            skLineSegment(sketch, "E349", {"start": v(-1.28, -1.8) * mm, "end": v(-1.4, -1.8) * mm});
            skLineSegment(sketch, "E350", {"start": v(-1.4, -1.8) * mm, "end": v(-1.45, -1.77) * mm});
            skLineSegment(sketch, "E351", {"start": v(-1.45, -1.77) * mm, "end": v(-1.48, -1.72) * mm});
            skLineSegment(sketch, "E352", {"start": v(-1.48, -1.72) * mm, "end": v(-1.47, -1.63) * mm});
            skLineSegment(sketch, "E353", {"start": v(-1.47, -1.63) * mm, "end": v(-1.43, -1.59) * mm});
            skLineSegment(sketch, "E354", {"start": v(-1.43, -1.59) * mm, "end": v(-1.38, -1.56) * mm});
            skLineSegment(sketch, "E355", {"start": v(-1.38, -1.56) * mm, "end": v(-1.32, -1.56) * mm});
            skLineSegment(sketch, "E356", {"start": v(-1.86, -1.56) * mm, "end": v(-1.81, -1.59) * mm});
            skLineSegment(sketch, "E357", {"start": v(-1.81, -1.59) * mm, "end": v(-1.79, -1.6) * mm});
            skLineSegment(sketch, "E358", {"start": v(-1.79, -1.6) * mm, "end": v(-1.77, -1.65) * mm});
            skLineSegment(sketch, "E359", {"start": v(-1.77, -1.65) * mm, "end": v(-1.77, -1.7) * mm});
            skLineSegment(sketch, "E360", {"start": v(-1.77, -1.7) * mm, "end": v(-1.94, -1.7) * mm});
            skLineSegment(sketch, "E361", {"start": v(-1.94, -1.7) * mm, "end": v(-1.92, -1.75) * mm});
            skLineSegment(sketch, "E362", {"start": v(-1.92, -1.75) * mm, "end": v(-1.9, -1.75) * mm});
            skLineSegment(sketch, "E363", {"start": v(-1.9, -1.75) * mm, "end": v(-1.86, -1.75) * mm});
            skLineSegment(sketch, "E364", {"start": v(-1.86, -1.75) * mm, "end": v(-1.85, -1.73) * mm});
            skLineSegment(sketch, "E365", {"start": v(-1.85, -1.73) * mm, "end": v(-1.77, -1.73) * mm});
            skLineSegment(sketch, "E366", {"start": v(-1.77, -1.73) * mm, "end": v(-1.78, -1.77) * mm});
            skLineSegment(sketch, "E367", {"start": v(-1.78, -1.77) * mm, "end": v(-1.83, -1.8) * mm});
            skLineSegment(sketch, "E368", {"start": v(-1.83, -1.8) * mm, "end": v(-1.95, -1.8) * mm});
            skLineSegment(sketch, "E369", {"start": v(-1.95, -1.8) * mm, "end": v(-2, -1.77) * mm});
            skLineSegment(sketch, "E370", {"start": v(-2, -1.77) * mm, "end": v(-2.02, -1.72) * mm});
            skLineSegment(sketch, "E371", {"start": v(-2.02, -1.72) * mm, "end": v(-2.02, -1.63) * mm});
            skLineSegment(sketch, "E372", {"start": v(-2.02, -1.63) * mm, "end": v(-1.98, -1.59) * mm});
            skLineSegment(sketch, "E373", {"start": v(-1.98, -1.59) * mm, "end": v(-1.92, -1.56) * mm});
            skLineSegment(sketch, "E374", {"start": v(-1.92, -1.56) * mm, "end": v(-1.86, -1.56) * mm});
            skLineSegment(sketch, "E375", {"start": v(-2.65, -1.56) * mm, "end": v(-2.6, -1.59) * mm});
            skLineSegment(sketch, "E376", {"start": v(-2.6, -1.59) * mm, "end": v(-2.57, -1.62) * mm});
            skLineSegment(sketch, "E377", {"start": v(-2.57, -1.62) * mm, "end": v(-2.55, -1.65) * mm});
            skLineSegment(sketch, "E378", {"start": v(-2.55, -1.65) * mm, "end": v(-2.55, -1.7) * mm});
            skLineSegment(sketch, "E379", {"start": v(-2.55, -1.7) * mm, "end": v(-2.73, -1.7) * mm});
            skLineSegment(sketch, "E380", {"start": v(-2.73, -1.7) * mm, "end": v(-2.71, -1.75) * mm});
            skLineSegment(sketch, "E381", {"start": v(-2.71, -1.75) * mm, "end": v(-2.7, -1.75) * mm});
            skLineSegment(sketch, "E382", {"start": v(-2.7, -1.75) * mm, "end": v(-2.65, -1.75) * mm});
            skLineSegment(sketch, "E383", {"start": v(-2.65, -1.75) * mm, "end": v(-2.64, -1.73) * mm});
            skLineSegment(sketch, "E384", {"start": v(-2.64, -1.73) * mm, "end": v(-2.55, -1.73) * mm});
            skLineSegment(sketch, "E385", {"start": v(-2.55, -1.73) * mm, "end": v(-2.57, -1.77) * mm});
            skLineSegment(sketch, "E386", {"start": v(-2.57, -1.77) * mm, "end": v(-2.61, -1.8) * mm});
            skLineSegment(sketch, "E387", {"start": v(-2.61, -1.8) * mm, "end": v(-2.73, -1.8) * mm});
            skLineSegment(sketch, "E388", {"start": v(-2.73, -1.8) * mm, "end": v(-2.79, -1.77) * mm});
            skLineSegment(sketch, "E389", {"start": v(-2.79, -1.77) * mm, "end": v(-2.81, -1.72) * mm});
            skLineSegment(sketch, "E390", {"start": v(-2.81, -1.72) * mm, "end": v(-2.8, -1.63) * mm});
            skLineSegment(sketch, "E391", {"start": v(-2.8, -1.63) * mm, "end": v(-2.77, -1.59) * mm});
            skLineSegment(sketch, "E392", {"start": v(-2.77, -1.59) * mm, "end": v(-2.71, -1.56) * mm});
            skLineSegment(sketch, "E393", {"start": v(-2.71, -1.56) * mm, "end": v(-2.65, -1.56) * mm});
            skLineSegment(sketch, "E394", {"start": v(-2.92, -1.56) * mm, "end": v(-2.87, -1.6) * mm});
            skLineSegment(sketch, "E395", {"start": v(-2.87, -1.6) * mm, "end": v(-2.84, -1.64) * mm});
            skLineSegment(sketch, "E396", {"start": v(-2.84, -1.64) * mm, "end": v(-2.84, -1.75) * mm});
            skLineSegment(sketch, "E397", {"start": v(-2.84, -1.75) * mm, "end": v(-2.89, -1.8) * mm});
            skLineSegment(sketch, "E398", {"start": v(-2.89, -1.8) * mm, "end": v(-2.98, -1.81) * mm});
            skLineSegment(sketch, "E399", {"start": v(-2.98, -1.81) * mm, "end": v(-3.03, -1.78) * mm});
            skLineSegment(sketch, "E400", {"start": v(-3.03, -1.78) * mm, "end": v(-3.03, -1.83) * mm});
            skLineSegment(sketch, "E401", {"start": v(-3.03, -1.83) * mm, "end": v(-3.11, -1.83) * mm});
            skLineSegment(sketch, "E402", {"start": v(-3.11, -1.83) * mm, "end": v(-3.11, -1.57) * mm});
            skLineSegment(sketch, "E403", {"start": v(-3.11, -1.57) * mm, "end": v(-3.03, -1.57) * mm});
            skLineSegment(sketch, "E404", {"start": v(-3.03, -1.57) * mm, "end": v(-3.02, -1.6) * mm});
            skLineSegment(sketch, "E405", {"start": v(-3.02, -1.6) * mm, "end": v(-3, -1.57) * mm});
            skLineSegment(sketch, "E406", {"start": v(-3, -1.57) * mm, "end": v(-2.92, -1.56) * mm});
            skLineSegment(sketch, "E407", {"start": v(-3.48, -1.5) * mm, "end": v(-3.48, -1.57) * mm});
            skLineSegment(sketch, "E408", {"start": v(-3.48, -1.57) * mm, "end": v(-3.35, -1.57) * mm});
            skLineSegment(sketch, "E409", {"start": v(-3.35, -1.57) * mm, "end": v(-3.3, -1.69) * mm});
            skLineSegment(sketch, "E410", {"start": v(-3.3, -1.69) * mm, "end": v(-3.27, -1.68) * mm});
            skLineSegment(sketch, "E411", {"start": v(-3.27, -1.68) * mm, "end": v(-3.23, -1.57) * mm});
            skLineSegment(sketch, "E412", {"start": v(-3.23, -1.57) * mm, "end": v(-3.13, -1.57) * mm});
            skLineSegment(sketch, "E413", {"start": v(-3.13, -1.57) * mm, "end": v(-3.21, -1.73) * mm});
            skLineSegment(sketch, "E414", {"start": v(-3.21, -1.73) * mm, "end": v(-3.27, -1.83) * mm});
            skLineSegment(sketch, "E415", {"start": v(-3.27, -1.83) * mm, "end": v(-3.36, -1.82) * mm});
            skLineSegment(sketch, "E416", {"start": v(-3.36, -1.82) * mm, "end": v(-3.33, -1.77) * mm});
            skLineSegment(sketch, "E417", {"start": v(-3.33, -1.77) * mm, "end": v(-3.44, -1.6) * mm});
            skLineSegment(sketch, "E418", {"start": v(-3.44, -1.6) * mm, "end": v(-3.44, -1.64) * mm});
            skLineSegment(sketch, "E419", {"start": v(-3.44, -1.64) * mm, "end": v(-3.48, -1.64) * mm});
            skLineSegment(sketch, "E420", {"start": v(-3.48, -1.64) * mm, "end": v(-3.48, -1.8) * mm});
            skLineSegment(sketch, "E421", {"start": v(-3.48, -1.8) * mm, "end": v(-3.57, -1.8) * mm});
            skLineSegment(sketch, "E422", {"start": v(-3.57, -1.8) * mm, "end": v(-3.57, -1.64) * mm});
            skLineSegment(sketch, "E423", {"start": v(-3.57, -1.64) * mm, "end": v(-3.6, -1.64) * mm});
            skLineSegment(sketch, "E424", {"start": v(-3.6, -1.64) * mm, "end": v(-3.6, -1.57) * mm});
            skLineSegment(sketch, "E425", {"start": v(-3.6, -1.57) * mm, "end": v(-3.57, -1.57) * mm});
            skLineSegment(sketch, "E426", {"start": v(-3.57, -1.57) * mm, "end": v(-3.57, -1.5) * mm});
            skLineSegment(sketch, "E427", {"start": v(-3.57, -1.5) * mm, "end": v(-3.48, -1.5) * mm});
            skLineSegment(sketch, "E428", {"start": v(-3.72, -1.56) * mm, "end": v(-3.65, -1.6) * mm});
            skLineSegment(sketch, "E429", {"start": v(-3.65, -1.6) * mm, "end": v(-3.62, -1.64) * mm});
            skLineSegment(sketch, "E430", {"start": v(-3.62, -1.64) * mm, "end": v(-3.62, -1.74) * mm});
            skLineSegment(sketch, "E431", {"start": v(-3.62, -1.74) * mm, "end": v(-3.67, -1.8) * mm});
            skLineSegment(sketch, "E432", {"start": v(-3.67, -1.8) * mm, "end": v(-3.72, -1.81) * mm});
            skLineSegment(sketch, "E433", {"start": v(-3.72, -1.81) * mm, "end": v(-3.82, -1.8) * mm});
            skLineSegment(sketch, "E434", {"start": v(-3.82, -1.8) * mm, "end": v(-3.89, -1.75) * mm});
            skLineSegment(sketch, "E435", {"start": v(-3.89, -1.75) * mm, "end": v(-3.9, -1.66) * mm});
            skLineSegment(sketch, "E436", {"start": v(-3.9, -1.66) * mm, "end": v(-3.87, -1.6) * mm});
            skLineSegment(sketch, "E437", {"start": v(-3.87, -1.6) * mm, "end": v(-3.82, -1.57) * mm});
            skLineSegment(sketch, "E438", {"start": v(-3.82, -1.57) * mm, "end": v(-3.72, -1.56) * mm});
            skLineSegment(sketch, "E439", {"start": v(-3.95, -1.5) * mm, "end": v(-3.95, -1.57) * mm});
            skLineSegment(sketch, "E440", {"start": v(-3.95, -1.57) * mm, "end": v(-3.9, -1.57) * mm});
            skLineSegment(sketch, "E441", {"start": v(-3.9, -1.57) * mm, "end": v(-3.9, -1.64) * mm});
            skLineSegment(sketch, "E442", {"start": v(-3.9, -1.64) * mm, "end": v(-3.95, -1.64) * mm});
            skLineSegment(sketch, "E443", {"start": v(-3.95, -1.64) * mm, "end": v(-3.95, -1.8) * mm});
            skLineSegment(sketch, "E444", {"start": v(-3.95, -1.8) * mm, "end": v(-4.03, -1.8) * mm});
            skLineSegment(sketch, "E445", {"start": v(-4.03, -1.8) * mm, "end": v(-4.03, -1.64) * mm});
            skLineSegment(sketch, "E446", {"start": v(-4.03, -1.64) * mm, "end": v(-4.06, -1.64) * mm});
            skLineSegment(sketch, "E447", {"start": v(-4.06, -1.64) * mm, "end": v(-4.06, -1.57) * mm});
            skLineSegment(sketch, "E448", {"start": v(-4.06, -1.57) * mm, "end": v(-4.03, -1.57) * mm});
            skLineSegment(sketch, "E449", {"start": v(-4.03, -1.57) * mm, "end": v(-4.03, -1.5) * mm});
            skLineSegment(sketch, "E450", {"start": v(-4.03, -1.5) * mm, "end": v(-3.95, -1.5) * mm});
            skLineSegment(sketch, "E451", {"start": v(-4.19, -1.56) * mm, "end": v(-4.12, -1.6) * mm});
            skLineSegment(sketch, "E452", {"start": v(-4.12, -1.6) * mm, "end": v(-4.1, -1.64) * mm});
            skLineSegment(sketch, "E453", {"start": v(-4.1, -1.64) * mm, "end": v(-4.1, -1.74) * mm});
            skLineSegment(sketch, "E454", {"start": v(-4.1, -1.74) * mm, "end": v(-4.14, -1.8) * mm});
            skLineSegment(sketch, "E455", {"start": v(-4.14, -1.8) * mm, "end": v(-4.19, -1.81) * mm});
            skLineSegment(sketch, "E456", {"start": v(-4.19, -1.81) * mm, "end": v(-4.29, -1.8) * mm});
            skLineSegment(sketch, "E457", {"start": v(-4.29, -1.8) * mm, "end": v(-4.36, -1.75) * mm});
            skLineSegment(sketch, "E458", {"start": v(-4.36, -1.75) * mm, "end": v(-4.37, -1.66) * mm});
            skLineSegment(sketch, "E459", {"start": v(-4.37, -1.66) * mm, "end": v(-4.34, -1.6) * mm});
            skLineSegment(sketch, "E460", {"start": v(-4.34, -1.6) * mm, "end": v(-4.29, -1.57) * mm});
            skLineSegment(sketch, "E461", {"start": v(-4.29, -1.57) * mm, "end": v(-4.19, -1.56) * mm});
            skLineSegment(sketch, "E462", {"start": v(4.79, -1.42) * mm, "end": v(4.8, -1.59) * mm});
            skLineSegment(sketch, "E463", {"start": v(4.8, -1.59) * mm, "end": v(4.84, -1.56) * mm});
            skLineSegment(sketch, "E464", {"start": v(4.84, -1.56) * mm, "end": v(4.9, -1.56) * mm});
            skLineSegment(sketch, "E465", {"start": v(4.9, -1.56) * mm, "end": v(4.95, -1.6) * mm});
            skLineSegment(sketch, "E466", {"start": v(4.95, -1.6) * mm, "end": v(4.98, -1.63) * mm});
            skLineSegment(sketch, "E467", {"start": v(4.98, -1.63) * mm, "end": v(4.98, -1.74) * mm});
            skLineSegment(sketch, "E468", {"start": v(4.98, -1.74) * mm, "end": v(4.93, -1.8) * mm});
            skLineSegment(sketch, "E469", {"start": v(4.93, -1.8) * mm, "end": v(4.84, -1.81) * mm});
            skLineSegment(sketch, "E470", {"start": v(4.84, -1.81) * mm, "end": v(4.79, -1.78) * mm});
            skLineSegment(sketch, "E471", {"start": v(4.79, -1.78) * mm, "end": v(4.79, -1.8) * mm});
            skLineSegment(sketch, "E472", {"start": v(4.79, -1.8) * mm, "end": v(4.7, -1.8) * mm});
            skLineSegment(sketch, "E473", {"start": v(4.7, -1.8) * mm, "end": v(4.7, -1.42) * mm});
            skLineSegment(sketch, "E474", {"start": v(4.7, -1.42) * mm, "end": v(4.79, -1.42) * mm});
            skLineSegment(sketch, "E475", {"start": v(3.03, -1.53) * mm, "end": v(2.97, -1.53) * mm});
            skLineSegment(sketch, "E476", {"start": v(2.97, -1.53) * mm, "end": v(2.97, -1.62) * mm});
            skLineSegment(sketch, "E477", {"start": v(2.97, -1.62) * mm, "end": v(3.05, -1.6) * mm});
            skLineSegment(sketch, "E478", {"start": v(3.05, -1.6) * mm, "end": v(3.05, -1.54) * mm});
            skLineSegment(sketch, "E479", {"start": v(3.05, -1.54) * mm, "end": v(3.03, -1.53) * mm});
            skLineSegment(sketch, "E480", {"start": v(-4.7, -1.53) * mm, "end": v(-4.77, -1.53) * mm});
            skLineSegment(sketch, "E481", {"start": v(-4.77, -1.53) * mm, "end": v(-4.77, -1.62) * mm});
            skLineSegment(sketch, "E482", {"start": v(-4.77, -1.62) * mm, "end": v(-4.69, -1.6) * mm});
            skLineSegment(sketch, "E483", {"start": v(-4.69, -1.6) * mm, "end": v(-4.69, -1.54) * mm});
            skLineSegment(sketch, "E484", {"start": v(-4.69, -1.54) * mm, "end": v(-4.7, -1.53) * mm});
            skLineSegment(sketch, "E485", {"start": v(3.36, -1.56) * mm, "end": v(3.36, -1.64) * mm});
            skLineSegment(sketch, "E486", {"start": v(3.36, -1.64) * mm, "end": v(3.29, -1.65) * mm});
            skLineSegment(sketch, "E487", {"start": v(3.29, -1.65) * mm, "end": v(3.27, -1.68) * mm});
            skLineSegment(sketch, "E488", {"start": v(3.27, -1.68) * mm, "end": v(3.27, -1.8) * mm});
            skLineSegment(sketch, "E489", {"start": v(3.27, -1.8) * mm, "end": v(3.19, -1.8) * mm});
            skLineSegment(sketch, "E490", {"start": v(3.19, -1.8) * mm, "end": v(3.19, -1.57) * mm});
            skLineSegment(sketch, "E491", {"start": v(3.19, -1.57) * mm, "end": v(3.27, -1.57) * mm});
            skLineSegment(sketch, "E492", {"start": v(3.27, -1.57) * mm, "end": v(3.28, -1.6) * mm});
            skLineSegment(sketch, "E493", {"start": v(3.28, -1.6) * mm, "end": v(3.3, -1.57) * mm});
            skLineSegment(sketch, "E494", {"start": v(3.3, -1.57) * mm, "end": v(3.36, -1.56) * mm});
            skLineSegment(sketch, "E495", {"start": v(-4.38, -1.56) * mm, "end": v(-4.38, -1.64) * mm});
            skLineSegment(sketch, "E496", {"start": v(-4.38, -1.64) * mm, "end": v(-4.45, -1.65) * mm});
            skLineSegment(sketch, "E497", {"start": v(-4.45, -1.65) * mm, "end": v(-4.47, -1.68) * mm});
            skLineSegment(sketch, "E498", {"start": v(-4.47, -1.68) * mm, "end": v(-4.47, -1.8) * mm});
            skLineSegment(sketch, "E499", {"start": v(-4.47, -1.8) * mm, "end": v(-4.55, -1.8) * mm});
            skLineSegment(sketch, "E500", {"start": v(-4.55, -1.8) * mm, "end": v(-4.55, -1.57) * mm});
            skLineSegment(sketch, "E501", {"start": v(-4.55, -1.57) * mm, "end": v(-4.47, -1.57) * mm});
            skLineSegment(sketch, "E502", {"start": v(-4.47, -1.57) * mm, "end": v(-4.46, -1.6) * mm});
            skLineSegment(sketch, "E503", {"start": v(-4.46, -1.6) * mm, "end": v(-4.44, -1.57) * mm});
            skLineSegment(sketch, "E504", {"start": v(-4.44, -1.57) * mm, "end": v(-4.38, -1.56) * mm});
            skLineSegment(sketch, "E505", {"start": v(4.26, -1.46) * mm, "end": v(4.26, -1.73) * mm});
            skLineSegment(sketch, "E506", {"start": v(4.26, -1.73) * mm, "end": v(4.36, -1.73) * mm});
            skLineSegment(sketch, "E507", {"start": v(4.36, -1.73) * mm, "end": v(4.36, -1.8) * mm});
            skLineSegment(sketch, "E508", {"start": v(4.36, -1.8) * mm, "end": v(4.17, -1.8) * mm});
            skLineSegment(sketch, "E509", {"start": v(4.17, -1.8) * mm, "end": v(4.17, -1.46) * mm});
            skLineSegment(sketch, "E510", {"start": v(4.17, -1.46) * mm, "end": v(4.26, -1.46) * mm});
            skLineSegment(sketch, "E511", {"start": v(2.52, -1.53) * mm, "end": v(2.46, -1.53) * mm});
            skLineSegment(sketch, "E512", {"start": v(2.46, -1.53) * mm, "end": v(2.46, -1.73) * mm});
            skLineSegment(sketch, "E513", {"start": v(2.46, -1.73) * mm, "end": v(2.54, -1.72) * mm});
            skLineSegment(sketch, "E514", {"start": v(2.54, -1.72) * mm, "end": v(2.57, -1.7) * mm});
            skLineSegment(sketch, "E515", {"start": v(2.57, -1.7) * mm, "end": v(2.58, -1.66) * mm});
            skLineSegment(sketch, "E516", {"start": v(2.58, -1.66) * mm, "end": v(2.58, -1.58) * mm});
            skLineSegment(sketch, "E517", {"start": v(2.58, -1.58) * mm, "end": v(2.55, -1.55) * mm});
            skLineSegment(sketch, "E518", {"start": v(2.55, -1.55) * mm, "end": v(2.52, -1.53) * mm});
            skLineSegment(sketch, "E519", {"start": v(-2.2, -1.53) * mm, "end": v(-2.26, -1.53) * mm});
            skLineSegment(sketch, "E520", {"start": v(-2.26, -1.53) * mm, "end": v(-2.26, -1.73) * mm});
            skLineSegment(sketch, "E521", {"start": v(-2.26, -1.73) * mm, "end": v(-2.18, -1.72) * mm});
            skLineSegment(sketch, "E522", {"start": v(-2.18, -1.72) * mm, "end": v(-2.15, -1.7) * mm});
            skLineSegment(sketch, "E523", {"start": v(-2.15, -1.7) * mm, "end": v(-2.14, -1.66) * mm});
            skLineSegment(sketch, "E524", {"start": v(-2.14, -1.66) * mm, "end": v(-2.14, -1.58) * mm});
            skLineSegment(sketch, "E525", {"start": v(-2.14, -1.58) * mm, "end": v(-2.17, -1.55) * mm});
            skLineSegment(sketch, "E526", {"start": v(-2.17, -1.55) * mm, "end": v(-2.2, -1.53) * mm});
            skLineSegment(sketch, "E527", {"start": v(3.48, -1.57) * mm, "end": v(3.48, -1.8) * mm});
            skLineSegment(sketch, "E528", {"start": v(3.48, -1.8) * mm, "end": v(3.4, -1.8) * mm});
            skLineSegment(sketch, "E529", {"start": v(3.4, -1.8) * mm, "end": v(3.4, -1.57) * mm});
            skLineSegment(sketch, "E530", {"start": v(3.4, -1.57) * mm, "end": v(3.48, -1.57) * mm});
            skLineSegment(sketch, "E531", {"start": v(1.84, -1.42) * mm, "end": v(1.84, -1.8) * mm});
            skLineSegment(sketch, "E532", {"start": v(1.84, -1.8) * mm, "end": v(1.76, -1.8) * mm});
            skLineSegment(sketch, "E533", {"start": v(1.76, -1.8) * mm, "end": v(1.75, -1.78) * mm});
            skLineSegment(sketch, "E534", {"start": v(1.75, -1.78) * mm, "end": v(1.73, -1.8) * mm});
            skLineSegment(sketch, "E535", {"start": v(1.73, -1.8) * mm, "end": v(1.64, -1.8) * mm});
            skLineSegment(sketch, "E536", {"start": v(1.64, -1.8) * mm, "end": v(1.58, -1.76) * mm});
            skLineSegment(sketch, "E537", {"start": v(1.58, -1.76) * mm, "end": v(1.57, -1.66) * mm});
            skLineSegment(sketch, "E538", {"start": v(1.57, -1.66) * mm, "end": v(1.6, -1.6) * mm});
            skLineSegment(sketch, "E539", {"start": v(1.6, -1.6) * mm, "end": v(1.64, -1.57) * mm});
            skLineSegment(sketch, "E540", {"start": v(1.64, -1.57) * mm, "end": v(1.73, -1.57) * mm});
            skLineSegment(sketch, "E541", {"start": v(1.73, -1.57) * mm, "end": v(1.76, -1.6) * mm});
            skLineSegment(sketch, "E542", {"start": v(1.76, -1.6) * mm, "end": v(1.76, -1.42) * mm});
            skLineSegment(sketch, "E543", {"start": v(1.76, -1.42) * mm, "end": v(1.84, -1.42) * mm});
            skLineSegment(sketch, "E544", {"start": v(-1.1, -1.42) * mm, "end": v(-1.1, -1.8) * mm});
            skLineSegment(sketch, "E545", {"start": v(-1.1, -1.8) * mm, "end": v(-1.17, -1.8) * mm});
            skLineSegment(sketch, "E546", {"start": v(-1.17, -1.8) * mm, "end": v(-1.17, -1.42) * mm});
            skLineSegment(sketch, "E547", {"start": v(-1.17, -1.42) * mm, "end": v(-1.1, -1.42) * mm});
            skLineSegment(sketch, "E548", {"start": v(-1.46, -1.57) * mm, "end": v(-1.56, -1.76) * mm});
            skLineSegment(sketch, "E549", {"start": v(-1.56, -1.76) * mm, "end": v(-1.58, -1.8) * mm});
            skLineSegment(sketch, "E550", {"start": v(-1.58, -1.8) * mm, "end": v(-1.64, -1.8) * mm});
            skLineSegment(sketch, "E551", {"start": v(-1.64, -1.8) * mm, "end": v(-1.67, -1.74) * mm});
            skLineSegment(sketch, "E552", {"start": v(-1.67, -1.74) * mm, "end": v(-1.73, -1.63) * mm});
            skLineSegment(sketch, "E553", {"start": v(-1.73, -1.63) * mm, "end": v(-1.77, -1.57) * mm});
            skLineSegment(sketch, "E554", {"start": v(-1.77, -1.57) * mm, "end": v(-1.67, -1.57) * mm});
            skLineSegment(sketch, "E555", {"start": v(-1.67, -1.57) * mm, "end": v(-1.62, -1.69) * mm});
            skLineSegment(sketch, "E556", {"start": v(-1.62, -1.69) * mm, "end": v(-1.6, -1.69) * mm});
            skLineSegment(sketch, "E557", {"start": v(-1.6, -1.69) * mm, "end": v(-1.56, -1.57) * mm});
            skLineSegment(sketch, "E558", {"start": v(-1.56, -1.57) * mm, "end": v(-1.46, -1.57) * mm});
            skLineSegment(sketch, "E559", {"start": v(-2.33, 0.16) * mm, "end": v(-2.14, 0.06) * mm});
            skLineSegment(sketch, "E560", {"start": v(-2.14, 0.06) * mm, "end": v(-2.11, 0.06) * mm});
            skLineSegment(sketch, "E561", {"start": v(-2.11, 0.06) * mm, "end": v(-1.92, -0.03) * mm});
            skLineSegment(sketch, "E562", {"start": v(-1.92, -0.03) * mm, "end": v(-1.9, -0.03) * mm});
            skLineSegment(sketch, "E563", {"start": v(-1.9, -0.03) * mm, "end": v(-1.83, -0.06) * mm});
            skLineSegment(sketch, "E564", {"start": v(-1.83, -0.06) * mm, "end": v(-1.8, -0.06) * mm});
            skLineSegment(sketch, "E565", {"start": v(-1.8, -0.06) * mm, "end": v(-1.7, -0.1) * mm});
            skLineSegment(sketch, "E566", {"start": v(-1.7, -0.1) * mm, "end": v(-1.69, -0.45) * mm});
            skLineSegment(sketch, "E567", {"start": v(-1.69, -0.45) * mm, "end": v(-1.2, -0.44) * mm});
            skLineSegment(sketch, "E568", {"start": v(-1.2, -0.44) * mm, "end": v(-1.02, -0.4) * mm});
            skLineSegment(sketch, "E569", {"start": v(-1.02, -0.4) * mm, "end": v(-0.95, -0.43) * mm});
            skLineSegment(sketch, "E570", {"start": v(-0.95, -0.43) * mm, "end": v(-0.92, -0.43) * mm});
            skLineSegment(sketch, "E571", {"start": v(-0.92, -0.43) * mm, "end": v(-0.86, -0.47) * mm});
            skLineSegment(sketch, "E572", {"start": v(-0.86, -0.47) * mm, "end": v(-0.83, -0.47) * mm});
            skLineSegment(sketch, "E573", {"start": v(-0.83, -0.47) * mm, "end": v(-0.77, -0.5) * mm});
            skLineSegment(sketch, "E574", {"start": v(-0.77, -0.5) * mm, "end": v(-0.74, -0.5) * mm});
            skLineSegment(sketch, "E575", {"start": v(-0.74, -0.5) * mm, "end": v(-0.55, -0.6) * mm});
            skLineSegment(sketch, "E576", {"start": v(-0.55, -0.6) * mm, "end": v(-0.52, -0.6) * mm});
            skLineSegment(sketch, "E577", {"start": v(-0.52, -0.6) * mm, "end": v(-0.33, -0.69) * mm});
            skLineSegment(sketch, "E578", {"start": v(-0.33, -0.69) * mm, "end": v(-0.3, -0.69) * mm});
            skLineSegment(sketch, "E579", {"start": v(-0.3, -0.69) * mm, "end": v(-0.26, -0.72) * mm});
            skLineSegment(sketch, "E580", {"start": v(-0.26, -0.72) * mm, "end": v(-0.3, -0.76) * mm});
            skLineSegment(sketch, "E581", {"start": v(-0.3, -0.76) * mm, "end": v(-0.34, -0.78) * mm});
            skLineSegment(sketch, "E582", {"start": v(-0.34, -0.78) * mm, "end": v(-0.42, -0.85) * mm});
            skLineSegment(sketch, "E583", {"start": v(-0.42, -0.85) * mm, "end": v(-0.54, -0.91) * mm});
            skLineSegment(sketch, "E584", {"start": v(-0.54, -0.91) * mm, "end": v(-0.6, -0.95) * mm});
            skLineSegment(sketch, "E585", {"start": v(-0.6, -0.95) * mm, "end": v(-0.67, -0.97) * mm});
            skLineSegment(sketch, "E586", {"start": v(-0.67, -0.97) * mm, "end": v(-0.84, -1.04) * mm});
            skLineSegment(sketch, "E587", {"start": v(-0.84, -1.04) * mm, "end": v(-1.1, -1.1) * mm});
            skLineSegment(sketch, "E588", {"start": v(-1.1, -1.1) * mm, "end": v(-2.34, 0.16) * mm});
            skLineSegment(sketch, "E589", {"start": v(-2.34, 0.16) * mm, "end": v(-2.33, 0.16) * mm});
            skLineSegment(sketch, "E590", {"start": v(-1.7, 0.2) * mm, "end": v(-1.7, -0.05) * mm});
            skLineSegment(sketch, "E591", {"start": v(-1.7, -0.05) * mm, "end": v(-1.85, 0) * mm});
            skLineSegment(sketch, "E592", {"start": v(-1.85, 0) * mm, "end": v(-2.33, 0.2) * mm});
            skLineSegment(sketch, "E593", {"start": v(-2.33, 0.2) * mm, "end": v(-1.7, 0.2) * mm});
            skLineSegment(sketch, "E594", {"start": v(0.1, 0.2) * mm, "end": v(0.08, -0.02) * mm});
            skLineSegment(sketch, "E595", {"start": v(0.08, -0.02) * mm, "end": v(0.05, -0.2) * mm});
            skLineSegment(sketch, "E596", {"start": v(0.05, -0.2) * mm, "end": v(0, -0.35) * mm});
            skLineSegment(sketch, "E597", {"start": v(0, -0.35) * mm, "end": v(-0.07, -0.47) * mm});
            skLineSegment(sketch, "E598", {"start": v(-0.07, -0.47) * mm, "end": v(-0.14, -0.59) * mm});
            skLineSegment(sketch, "E599", {"start": v(-0.14, -0.59) * mm, "end": v(-0.21, -0.67) * mm});
            skLineSegment(sketch, "E600", {"start": v(-0.21, -0.67) * mm, "end": v(-0.7, -0.47) * mm});
            skLineSegment(sketch, "E601", {"start": v(-0.7, -0.47) * mm, "end": v(-0.96, -0.36) * mm});
            skLineSegment(sketch, "E602", {"start": v(-0.96, -0.36) * mm, "end": v(-0.94, -0.34) * mm});
            skLineSegment(sketch, "E603", {"start": v(-0.94, -0.34) * mm, "end": v(-0.9, -0.32) * mm});
            skLineSegment(sketch, "E604", {"start": v(-0.9, -0.32) * mm, "end": v(-0.81, -0.23) * mm});
            skLineSegment(sketch, "E605", {"start": v(-0.81, -0.23) * mm, "end": v(-0.8, -0.2) * mm});
            skLineSegment(sketch, "E606", {"start": v(-0.8, -0.2) * mm, "end": v(-0.74, -0.12) * mm});
            skLineSegment(sketch, "E607", {"start": v(-0.74, -0.12) * mm, "end": v(-0.7, 0.01) * mm});
            skLineSegment(sketch, "E608", {"start": v(-0.7, 0.01) * mm, "end": v(-0.67, 0.2) * mm});
            skLineSegment(sketch, "E609", {"start": v(-0.67, 0.2) * mm, "end": v(0.1, 0.2) * mm});
            skLineSegment(sketch, "E610", {"start": v(-2.44, 0.18) * mm, "end": v(-1.17, -1.1) * mm});
            skLineSegment(sketch, "E611", {"start": v(-1.17, -1.1) * mm, "end": v(-1.3, -1.12) * mm});
            skLineSegment(sketch, "E612", {"start": v(-1.3, -1.12) * mm, "end": v(-2.43, -1.1) * mm});
            skLineSegment(sketch, "E613", {"start": v(-2.43, -1.1) * mm, "end": v(-2.45, 0.18) * mm});
            skLineSegment(sketch, "E614", {"start": v(-2.45, 0.18) * mm, "end": v(-2.44, 0.18) * mm});
            skLineSegment(sketch, "E615", {"start": v(-1.71, 0.51) * mm, "end": v(-1.7, 0.25) * mm});
            skLineSegment(sketch, "E616", {"start": v(-1.7, 0.25) * mm, "end": v(-2.3, 0.26) * mm});
            skLineSegment(sketch, "E617", {"start": v(-2.3, 0.26) * mm, "end": v(-2.23, 0.3) * mm});
            skLineSegment(sketch, "E618", {"start": v(-2.23, 0.3) * mm, "end": v(-2.14, 0.33) * mm});
            skLineSegment(sketch, "E619", {"start": v(-2.14, 0.33) * mm, "end": v(-1.71, 0.51) * mm});
            skLineSegment(sketch, "E620", {"start": v(-4.08, 0.76) * mm, "end": v(-4.19, 0.76) * mm});
            skLineSegment(sketch, "E621", {"start": v(-4.19, 0.76) * mm, "end": v(-4.21, 0.72) * mm});
            skLineSegment(sketch, "E622", {"start": v(-4.21, 0.72) * mm, "end": v(-4.23, 0.72) * mm});
            skLineSegment(sketch, "E623", {"start": v(-4.23, 0.72) * mm, "end": v(-4.22, 0.53) * mm});
            skLineSegment(sketch, "E624", {"start": v(-4.22, 0.53) * mm, "end": v(-4.21, 0.53) * mm});
            skLineSegment(sketch, "E625", {"start": v(-4.21, 0.53) * mm, "end": v(-4.19, 0.5) * mm});
            skLineSegment(sketch, "E626", {"start": v(-4.19, 0.5) * mm, "end": v(-4.08, 0.5) * mm});
            skLineSegment(sketch, "E627", {"start": v(-4.08, 0.5) * mm, "end": v(-4.08, 0.76) * mm});
            skLineSegment(sketch, "E628", {"start": v(0.86, 0.8) * mm, "end": v(0.8, 0.8) * mm});
            skLineSegment(sketch, "E629", {"start": v(0.8, 0.8) * mm, "end": v(0.76, 0.74) * mm});
            skLineSegment(sketch, "E630", {"start": v(0.76, 0.74) * mm, "end": v(0.71, 0.7) * mm});
            skLineSegment(sketch, "E631", {"start": v(0.71, 0.7) * mm, "end": v(0.69, 0.66) * mm});
            skLineSegment(sketch, "E632", {"start": v(0.69, 0.66) * mm, "end": v(0.62, 0.6) * mm});
            skLineSegment(sketch, "E633", {"start": v(0.62, 0.6) * mm, "end": v(0.6, 0.56) * mm});
            skLineSegment(sketch, "E634", {"start": v(0.6, 0.56) * mm, "end": v(0.6, 0.53) * mm});
            skLineSegment(sketch, "E635", {"start": v(0.6, 0.53) * mm, "end": v(0.6, 0.53) * mm});
            skLineSegment(sketch, "E636", {"start": v(0.6, 0.53) * mm, "end": v(0.67, 0.34) * mm});
            skLineSegment(sketch, "E637", {"start": v(0.67, 0.34) * mm, "end": v(0.67, 0.34) * mm});
            skLineSegment(sketch, "E638", {"start": v(0.67, 0.34) * mm, "end": v(0.69, 0.28) * mm});
            skLineSegment(sketch, "E639", {"start": v(0.69, 0.28) * mm, "end": v(0.77, 0.28) * mm});
            skLineSegment(sketch, "E640", {"start": v(0.77, 0.28) * mm, "end": v(1.02, 0.24) * mm});
            skLineSegment(sketch, "E641", {"start": v(1.02, 0.24) * mm, "end": v(1.17, 0.18) * mm});
            skLineSegment(sketch, "E642", {"start": v(1.17, 0.18) * mm, "end": v(1.26, 0.1) * mm});
            skLineSegment(sketch, "E643", {"start": v(1.26, 0.1) * mm, "end": v(1.32, 0.01) * mm});
            skLineSegment(sketch, "E644", {"start": v(1.32, 0.01) * mm, "end": v(1.33, -0.06) * mm});
            skLineSegment(sketch, "E645", {"start": v(1.33, -0.06) * mm, "end": v(1.33, -0.2) * mm});
            skLineSegment(sketch, "E646", {"start": v(1.33, -0.2) * mm, "end": v(1.3, -0.28) * mm});
            skLineSegment(sketch, "E647", {"start": v(1.3, -0.28) * mm, "end": v(1.25, -0.33) * mm});
            skLineSegment(sketch, "E648", {"start": v(1.25, -0.33) * mm, "end": v(1.17, -0.37) * mm});
            skLineSegment(sketch, "E649", {"start": v(1.17, -0.37) * mm, "end": v(0.97, -0.38) * mm});
            skLineSegment(sketch, "E650", {"start": v(0.97, -0.38) * mm, "end": v(0.81, -0.34) * mm});
            skLineSegment(sketch, "E651", {"start": v(0.81, -0.34) * mm, "end": v(0.67, -0.28) * mm});
            skLineSegment(sketch, "E652", {"start": v(0.67, -0.28) * mm, "end": v(0.57, -0.2) * mm});
            skLineSegment(sketch, "E653", {"start": v(0.57, -0.2) * mm, "end": v(0.48, -0.1) * mm});
            skLineSegment(sketch, "E654", {"start": v(0.48, -0.1) * mm, "end": v(0.44, -0.13) * mm});
            skLineSegment(sketch, "E655", {"start": v(0.44, -0.13) * mm, "end": v(0.36, -0.23) * mm});
            skLineSegment(sketch, "E656", {"start": v(0.36, -0.23) * mm, "end": v(0.32, -0.28) * mm});
            skLineSegment(sketch, "E657", {"start": v(0.32, -0.28) * mm, "end": v(0.3, -0.31) * mm});
            skLineSegment(sketch, "E658", {"start": v(0.3, -0.31) * mm, "end": v(0.24, -0.37) * mm});
            skLineSegment(sketch, "E659", {"start": v(0.24, -0.37) * mm, "end": v(0.22, -0.4) * mm});
            skLineSegment(sketch, "E660", {"start": v(0.22, -0.4) * mm, "end": v(0.2, -0.43) * mm});
            skLineSegment(sketch, "E661", {"start": v(0.2, -0.43) * mm, "end": v(0.21, -0.43) * mm});
            skLineSegment(sketch, "E662", {"start": v(0.21, -0.43) * mm, "end": v(0.23, -0.46) * mm});
            skLineSegment(sketch, "E663", {"start": v(0.23, -0.46) * mm, "end": v(0.23, -0.46) * mm});
            skLineSegment(sketch, "E664", {"start": v(0.23, -0.46) * mm, "end": v(0.33, -0.56) * mm});
            skLineSegment(sketch, "E665", {"start": v(0.33, -0.56) * mm, "end": v(0.34, -0.56) * mm});
            skLineSegment(sketch, "E666", {"start": v(0.34, -0.56) * mm, "end": v(0.36, -0.59) * mm});
            skLineSegment(sketch, "E667", {"start": v(0.36, -0.59) * mm, "end": v(0.38, -0.59) * mm});
            skLineSegment(sketch, "E668", {"start": v(0.38, -0.59) * mm, "end": v(0.45, -0.65) * mm});
            skLineSegment(sketch, "E669", {"start": v(0.45, -0.65) * mm, "end": v(0.46, -0.65) * mm});
            skLineSegment(sketch, "E670", {"start": v(0.46, -0.65) * mm, "end": v(0.55, -0.7) * mm});
            skLineSegment(sketch, "E671", {"start": v(0.55, -0.7) * mm, "end": v(0.57, -0.7) * mm});
            skLineSegment(sketch, "E672", {"start": v(0.57, -0.7) * mm, "end": v(0.63, -0.75) * mm});
            skLineSegment(sketch, "E673", {"start": v(0.63, -0.75) * mm, "end": v(0.65, -0.75) * mm});
            skLineSegment(sketch, "E674", {"start": v(0.65, -0.75) * mm, "end": v(0.7, -0.78) * mm});
            skLineSegment(sketch, "E675", {"start": v(0.7, -0.78) * mm, "end": v(0.73, -0.78) * mm});
            skLineSegment(sketch, "E676", {"start": v(0.73, -0.78) * mm, "end": v(0.83, -0.81) * mm});
            skLineSegment(sketch, "E677", {"start": v(0.83, -0.81) * mm, "end": v(0.86, -0.81) * mm});
            skLineSegment(sketch, "E678", {"start": v(0.86, -0.81) * mm, "end": v(0.97, -0.84) * mm});
            skLineSegment(sketch, "E679", {"start": v(0.97, -0.84) * mm, "end": v(1.05, -0.84) * mm});
            skLineSegment(sketch, "E680", {"start": v(1.05, -0.84) * mm, "end": v(1.16, -0.85) * mm});
            skLineSegment(sketch, "E681", {"start": v(1.16, -0.85) * mm, "end": v(1.36, -0.81) * mm});
            skLineSegment(sketch, "E682", {"start": v(1.36, -0.81) * mm, "end": v(1.55, -0.73) * mm});
            skLineSegment(sketch, "E683", {"start": v(1.55, -0.73) * mm, "end": v(1.66, -0.64) * mm});
            skLineSegment(sketch, "E684", {"start": v(1.66, -0.64) * mm, "end": v(1.73, -0.53) * mm});
            skLineSegment(sketch, "E685", {"start": v(1.73, -0.53) * mm, "end": v(1.79, -0.4) * mm});
            skLineSegment(sketch, "E686", {"start": v(1.79, -0.4) * mm, "end": v(1.81, -0.27) * mm});
            skLineSegment(sketch, "E687", {"start": v(1.81, -0.27) * mm, "end": v(1.8, -0.06) * mm});
            skLineSegment(sketch, "E688", {"start": v(1.8, -0.06) * mm, "end": v(1.77, 0.1) * mm});
            skLineSegment(sketch, "E689", {"start": v(1.77, 0.1) * mm, "end": v(1.71, 0.2) * mm});
            skLineSegment(sketch, "E690", {"start": v(1.71, 0.2) * mm, "end": v(1.65, 0.3) * mm});
            skLineSegment(sketch, "E691", {"start": v(1.65, 0.3) * mm, "end": v(1.55, 0.4) * mm});
            skLineSegment(sketch, "E692", {"start": v(1.55, 0.4) * mm, "end": v(1.52, 0.43) * mm});
            skLineSegment(sketch, "E693", {"start": v(1.52, 0.43) * mm, "end": v(1.45, 0.47) * mm});
            skLineSegment(sketch, "E694", {"start": v(1.45, 0.47) * mm, "end": v(1.3, 0.55) * mm});
            skLineSegment(sketch, "E695", {"start": v(1.3, 0.55) * mm, "end": v(1.18, 0.58) * mm});
            skLineSegment(sketch, "E696", {"start": v(1.18, 0.58) * mm, "end": v(1.11, 0.59) * mm});
            skLineSegment(sketch, "E697", {"start": v(1.11, 0.59) * mm, "end": v(1.3, 0.78) * mm});
            skLineSegment(sketch, "E698", {"start": v(1.3, 0.78) * mm, "end": v(0.86, 0.8) * mm});
            skLineSegment(sketch, "E699", {"start": v(3.45, 0.78) * mm, "end": v(3.5, -0.14) * mm});
            skLineSegment(sketch, "E700", {"start": v(3.5, -0.14) * mm, "end": v(3.52, -0.14) * mm});
            skLineSegment(sketch, "E701", {"start": v(3.52, -0.14) * mm, "end": v(3.64, -0.16) * mm});
            skLineSegment(sketch, "E702", {"start": v(3.64, -0.16) * mm, "end": v(3.69, -0.08) * mm});
            skLineSegment(sketch, "E703", {"start": v(3.69, -0.08) * mm, "end": v(3.72, 0.03) * mm});
            skLineSegment(sketch, "E704", {"start": v(3.72, 0.03) * mm, "end": v(3.72, 0.34) * mm});
            skLineSegment(sketch, "E705", {"start": v(3.72, 0.34) * mm, "end": v(3.67, 0.5) * mm});
            skLineSegment(sketch, "E706", {"start": v(3.67, 0.5) * mm, "end": v(3.63, 0.59) * mm});
            skLineSegment(sketch, "E707", {"start": v(3.63, 0.59) * mm, "end": v(3.56, 0.68) * mm});
            skLineSegment(sketch, "E708", {"start": v(3.56, 0.68) * mm, "end": v(3.5, 0.75) * mm});
            skLineSegment(sketch, "E709", {"start": v(3.5, 0.75) * mm, "end": v(3.46, 0.76) * mm});
            skLineSegment(sketch, "E710", {"start": v(3.46, 0.76) * mm, "end": v(3.45, 0.78) * mm});
            skLineSegment(sketch, "E711", {"start": v(3.11, 0.97) * mm, "end": v(3.28, 0.94) * mm});
            skLineSegment(sketch, "E712", {"start": v(3.28, 0.94) * mm, "end": v(3.44, 0.87) * mm});
            skLineSegment(sketch, "E713", {"start": v(3.44, 0.87) * mm, "end": v(3.53, 0.8) * mm});
            skLineSegment(sketch, "E714", {"start": v(3.53, 0.8) * mm, "end": v(3.64, 0.7) * mm});
            skLineSegment(sketch, "E715", {"start": v(3.64, 0.7) * mm, "end": v(3.73, 0.56) * mm});
            skLineSegment(sketch, "E716", {"start": v(3.73, 0.56) * mm, "end": v(3.78, 0.4) * mm});
            skLineSegment(sketch, "E717", {"start": v(3.78, 0.4) * mm, "end": v(3.8, 0.3) * mm});
            skLineSegment(sketch, "E718", {"start": v(3.8, 0.3) * mm, "end": v(3.79, 0.01) * mm});
            skLineSegment(sketch, "E719", {"start": v(3.79, 0.01) * mm, "end": v(3.75, -0.12) * mm});
            skLineSegment(sketch, "E720", {"start": v(3.75, -0.12) * mm, "end": v(3.69, -0.22) * mm});
            skLineSegment(sketch, "E721", {"start": v(3.69, -0.22) * mm, "end": v(3.63, -0.3) * mm});
            skLineSegment(sketch, "E722", {"start": v(3.63, -0.3) * mm, "end": v(3.6, -0.3) * mm});
            skLineSegment(sketch, "E723", {"start": v(3.6, -0.3) * mm, "end": v(3.52, -0.36) * mm});
            skLineSegment(sketch, "E724", {"start": v(3.52, -0.36) * mm, "end": v(3.4, -0.4) * mm});
            skLineSegment(sketch, "E725", {"start": v(3.4, -0.4) * mm, "end": v(3.16, -0.4) * mm});
            skLineSegment(sketch, "E726", {"start": v(3.16, -0.4) * mm, "end": v(2.93, -0.37) * mm});
            skLineSegment(sketch, "E727", {"start": v(2.93, -0.37) * mm, "end": v(2.82, 0.97) * mm});
            skLineSegment(sketch, "E728", {"start": v(2.82, 0.97) * mm, "end": v(3.11, 0.97) * mm});
            skLineSegment(sketch, "E729", {"start": v(-3.58, 0.94) * mm, "end": v(-4, 0.94) * mm});
            skLineSegment(sketch, "E730", {"start": v(-4, 0.94) * mm, "end": v(-4, 0.83) * mm});
            skLineSegment(sketch, "E731", {"start": v(-4, 0.83) * mm, "end": v(-3.84, 0.83) * mm});
            skLineSegment(sketch, "E732", {"start": v(-3.84, 0.83) * mm, "end": v(-3.84, 0.76) * mm});
            skLineSegment(sketch, "E733", {"start": v(-3.84, 0.76) * mm, "end": v(-4, 0.76) * mm});
            skLineSegment(sketch, "E734", {"start": v(-4, 0.76) * mm, "end": v(-4, 0.5) * mm});
            skLineSegment(sketch, "E735", {"start": v(-4, 0.5) * mm, "end": v(-3.84, 0.5) * mm});
            skLineSegment(sketch, "E736", {"start": v(-3.84, 0.5) * mm, "end": v(-3.84, 0.43) * mm});
            skLineSegment(sketch, "E737", {"start": v(-3.84, 0.43) * mm, "end": v(-4, 0.43) * mm});
            skLineSegment(sketch, "E738", {"start": v(-4, 0.43) * mm, "end": v(-4, 0.32) * mm});
            skLineSegment(sketch, "E739", {"start": v(-4, 0.32) * mm, "end": v(-3.53, 0.33) * mm});
            skLineSegment(sketch, "E740", {"start": v(-3.53, 0.33) * mm, "end": v(-3.45, 0.37) * mm});
            skLineSegment(sketch, "E741", {"start": v(-3.45, 0.37) * mm, "end": v(-3.4, 0.42) * mm});
            skLineSegment(sketch, "E742", {"start": v(-3.4, 0.42) * mm, "end": v(-3.38, 0.45) * mm});
            skLineSegment(sketch, "E743", {"start": v(-3.38, 0.45) * mm, "end": v(-3.34, 0.51) * mm});
            skLineSegment(sketch, "E744", {"start": v(-3.34, 0.51) * mm, "end": v(-3.32, 0.66) * mm});
            skLineSegment(sketch, "E745", {"start": v(-3.32, 0.66) * mm, "end": v(-3.36, 0.77) * mm});
            skLineSegment(sketch, "E746", {"start": v(-3.36, 0.77) * mm, "end": v(-3.4, 0.84) * mm});
            skLineSegment(sketch, "E747", {"start": v(-3.4, 0.84) * mm, "end": v(-3.48, 0.9) * mm});
            skLineSegment(sketch, "E748", {"start": v(-3.48, 0.9) * mm, "end": v(-3.58, 0.94) * mm});
            skLineSegment(sketch, "E749", {"start": v(1.4, 1.2) * mm, "end": v(1.4, 1.12) * mm});
            skLineSegment(sketch, "E750", {"start": v(1.4, 1.12) * mm, "end": v(1.35, 1.12) * mm});
            skLineSegment(sketch, "E751", {"start": v(1.35, 1.12) * mm, "end": v(1.35, 1.2) * mm});
            skLineSegment(sketch, "E752", {"start": v(1.35, 1.2) * mm, "end": v(1.4, 1.2) * mm});
            skLineSegment(sketch, "E753", {"start": v(-4, 1.12) * mm, "end": v(-4, 1.01) * mm});
            skLineSegment(sketch, "E754", {"start": v(-4, 1.01) * mm, "end": v(-3.55, 1.01) * mm});
            skLineSegment(sketch, "E755", {"start": v(-3.55, 1.01) * mm, "end": v(-3.44, 0.97) * mm});
            skLineSegment(sketch, "E756", {"start": v(-3.44, 0.97) * mm, "end": v(-3.34, 0.88) * mm});
            skLineSegment(sketch, "E757", {"start": v(-3.34, 0.88) * mm, "end": v(-3.27, 0.77) * mm});
            skLineSegment(sketch, "E758", {"start": v(-3.27, 0.77) * mm, "end": v(-3.25, 0.69) * mm});
            skLineSegment(sketch, "E759", {"start": v(-3.25, 0.69) * mm, "end": v(-3.26, 0.53) * mm});
            skLineSegment(sketch, "E760", {"start": v(-3.26, 0.53) * mm, "end": v(-3.31, 0.41) * mm});
            skLineSegment(sketch, "E761", {"start": v(-3.31, 0.41) * mm, "end": v(-3.38, 0.33) * mm});
            skLineSegment(sketch, "E762", {"start": v(-3.38, 0.33) * mm, "end": v(-3.46, 0.28) * mm});
            skLineSegment(sketch, "E763", {"start": v(-3.46, 0.28) * mm, "end": v(-3.53, 0.25) * mm});
            skLineSegment(sketch, "E764", {"start": v(-3.53, 0.25) * mm, "end": v(-4, 0.25) * mm});
            skLineSegment(sketch, "E765", {"start": v(-4, 0.25) * mm, "end": v(-4, 0.13) * mm});
            skLineSegment(sketch, "E766", {"start": v(-4, 0.13) * mm, "end": v(-4.08, 0.13) * mm});
            skLineSegment(sketch, "E767", {"start": v(-4.08, 0.13) * mm, "end": v(-4.08, 0.43) * mm});
            skLineSegment(sketch, "E768", {"start": v(-4.08, 0.43) * mm, "end": v(-4.2, 0.42) * mm});
            skLineSegment(sketch, "E769", {"start": v(-4.2, 0.42) * mm, "end": v(-4.2, 0.4) * mm});
            skLineSegment(sketch, "E770", {"start": v(-4.2, 0.4) * mm, "end": v(-4.23, 0.38) * mm});
            skLineSegment(sketch, "E771", {"start": v(-4.23, 0.38) * mm, "end": v(-4.31, 0.4) * mm});
            skLineSegment(sketch, "E772", {"start": v(-4.31, 0.4) * mm, "end": v(-4.34, 0.43) * mm});
            skLineSegment(sketch, "E773", {"start": v(-4.34, 0.43) * mm, "end": v(-4.34, 0.5) * mm});
            skLineSegment(sketch, "E774", {"start": v(-4.34, 0.5) * mm, "end": v(-4.32, 0.53) * mm});
            skLineSegment(sketch, "E775", {"start": v(-4.32, 0.53) * mm, "end": v(-4.3, 0.54) * mm});
            skLineSegment(sketch, "E776", {"start": v(-4.3, 0.54) * mm, "end": v(-4.3, 0.72) * mm});
            skLineSegment(sketch, "E777", {"start": v(-4.3, 0.72) * mm, "end": v(-4.33, 0.73) * mm});
            skLineSegment(sketch, "E778", {"start": v(-4.33, 0.73) * mm, "end": v(-4.35, 0.8) * mm});
            skLineSegment(sketch, "E779", {"start": v(-4.35, 0.8) * mm, "end": v(-4.32, 0.86) * mm});
            skLineSegment(sketch, "E780", {"start": v(-4.32, 0.86) * mm, "end": v(-4.3, 0.87) * mm});
            skLineSegment(sketch, "E781", {"start": v(-4.3, 0.87) * mm, "end": v(-4.23, 0.87) * mm});
            skLineSegment(sketch, "E782", {"start": v(-4.23, 0.87) * mm, "end": v(-4.19, 0.84) * mm});
            skLineSegment(sketch, "E783", {"start": v(-4.19, 0.84) * mm, "end": v(-4.19, 0.83) * mm});
            skLineSegment(sketch, "E784", {"start": v(-4.19, 0.83) * mm, "end": v(-4.08, 0.83) * mm});
            skLineSegment(sketch, "E785", {"start": v(-4.08, 0.83) * mm, "end": v(-4.08, 1.12) * mm});
            skLineSegment(sketch, "E786", {"start": v(-4.08, 1.12) * mm, "end": v(-4, 1.12) * mm});
            skLineSegment(sketch, "E787", {"start": v(-0.24, 1.12) * mm, "end": v(-0.19, 1.06) * mm});
            skLineSegment(sketch, "E788", {"start": v(-0.19, 1.06) * mm, "end": v(-0.17, 1.03) * mm});
            skLineSegment(sketch, "E789", {"start": v(-0.17, 1.03) * mm, "end": v(-0.17, 1.03) * mm});
            skLineSegment(sketch, "E790", {"start": v(-0.17, 1.03) * mm, "end": v(-0.08, 0.9) * mm});
            skLineSegment(sketch, "E791", {"start": v(-0.08, 0.9) * mm, "end": v(-0.02, 0.8) * mm});
            skLineSegment(sketch, "E792", {"start": v(-0.02, 0.8) * mm, "end": v(0.05, 0.6) * mm});
            skLineSegment(sketch, "E793", {"start": v(0.05, 0.6) * mm, "end": v(0.1, 0.37) * mm});
            skLineSegment(sketch, "E794", {"start": v(0.1, 0.37) * mm, "end": v(0.1, 0.25) * mm});
            skLineSegment(sketch, "E795", {"start": v(0.1, 0.25) * mm, "end": v(-0.67, 0.25) * mm});
            skLineSegment(sketch, "E796", {"start": v(-0.67, 0.25) * mm, "end": v(-0.7, 0.42) * mm});
            skLineSegment(sketch, "E797", {"start": v(-0.7, 0.42) * mm, "end": v(-0.75, 0.56) * mm});
            skLineSegment(sketch, "E798", {"start": v(-0.75, 0.56) * mm, "end": v(-0.82, 0.65) * mm});
            skLineSegment(sketch, "E799", {"start": v(-0.82, 0.65) * mm, "end": v(-0.86, 0.7) * mm});
            skLineSegment(sketch, "E800", {"start": v(-0.86, 0.7) * mm, "end": v(-0.9, 0.72) * mm});
            skLineSegment(sketch, "E801", {"start": v(-0.9, 0.72) * mm, "end": v(-0.95, 0.76) * mm});
            skLineSegment(sketch, "E802", {"start": v(-0.95, 0.76) * mm, "end": v(-1.02, 0.8) * mm});
            skLineSegment(sketch, "E803", {"start": v(-1.02, 0.8) * mm, "end": v(-0.33, 1.08) * mm});
            skLineSegment(sketch, "E804", {"start": v(-0.33, 1.08) * mm, "end": v(-0.24, 1.12) * mm});
            skLineSegment(sketch, "E805", {"start": v(-1.1, 1.52) * mm, "end": v(-0.9, 1.47) * mm});
            skLineSegment(sketch, "E806", {"start": v(-0.9, 1.47) * mm, "end": v(-0.69, 1.4) * mm});
            skLineSegment(sketch, "E807", {"start": v(-0.69, 1.4) * mm, "end": v(-0.55, 1.34) * mm});
            skLineSegment(sketch, "E808", {"start": v(-0.55, 1.34) * mm, "end": v(-0.4, 1.25) * mm});
            skLineSegment(sketch, "E809", {"start": v(-0.4, 1.25) * mm, "end": v(-0.31, 1.18) * mm});
            skLineSegment(sketch, "E810", {"start": v(-0.31, 1.18) * mm, "end": v(-0.29, 1.16) * mm});
            skLineSegment(sketch, "E811", {"start": v(-0.29, 1.16) * mm, "end": v(-0.72, 0.98) * mm});
            skLineSegment(sketch, "E812", {"start": v(-0.72, 0.98) * mm, "end": v(-1.07, 0.83) * mm});
            skLineSegment(sketch, "E813", {"start": v(-1.07, 0.83) * mm, "end": v(-1.24, 0.87) * mm});
            skLineSegment(sketch, "E814", {"start": v(-1.24, 0.87) * mm, "end": v(-1.36, 0.9) * mm});
            skLineSegment(sketch, "E815", {"start": v(-1.36, 0.9) * mm, "end": v(-1.72, 0.9) * mm});
            skLineSegment(sketch, "E816", {"start": v(-1.72, 0.9) * mm, "end": v(-1.71, 0.56) * mm});
            skLineSegment(sketch, "E817", {"start": v(-1.71, 0.56) * mm, "end": v(-2, 0.45) * mm});
            skLineSegment(sketch, "E818", {"start": v(-2, 0.45) * mm, "end": v(-2.34, 0.3) * mm});
            skLineSegment(sketch, "E819", {"start": v(-2.34, 0.3) * mm, "end": v(-1.14, 1.52) * mm});
            skLineSegment(sketch, "E820", {"start": v(-1.14, 1.52) * mm, "end": v(-1.1, 1.52) * mm});
            skLineSegment(sketch, "E821", {"start": v(-3.6, 1.37) * mm, "end": v(-3.38, 1.34) * mm});
            skLineSegment(sketch, "E822", {"start": v(-3.38, 1.34) * mm, "end": v(-3.2, 1.27) * mm});
            skLineSegment(sketch, "E823", {"start": v(-3.2, 1.27) * mm, "end": v(-3.08, 1.2) * mm});
            skLineSegment(sketch, "E824", {"start": v(-3.08, 1.2) * mm, "end": v(-2.95, 1.08) * mm});
            skLineSegment(sketch, "E825", {"start": v(-2.95, 1.08) * mm, "end": v(-2.86, 0.95) * mm});
            skLineSegment(sketch, "E826", {"start": v(-2.86, 0.95) * mm, "end": v(-2.82, 0.82) * mm});
            skLineSegment(sketch, "E827", {"start": v(-2.82, 0.82) * mm, "end": v(-2.8, 0.73) * mm});
            skLineSegment(sketch, "E828", {"start": v(-2.8, 0.73) * mm, "end": v(-2.81, 0.5) * mm});
            skLineSegment(sketch, "E829", {"start": v(-2.81, 0.5) * mm, "end": v(-2.84, 0.4) * mm});
            skLineSegment(sketch, "E830", {"start": v(-2.84, 0.4) * mm, "end": v(-2.9, 0.28) * mm});
            skLineSegment(sketch, "E831", {"start": v(-2.9, 0.28) * mm, "end": v(-2.97, 0.19) * mm});
            skLineSegment(sketch, "E832", {"start": v(-2.97, 0.19) * mm, "end": v(-3.02, 0.13) * mm});
            skLineSegment(sketch, "E833", {"start": v(-3.02, 0.13) * mm, "end": v(-3.06, 0.1) * mm});
            skLineSegment(sketch, "E834", {"start": v(-3.06, 0.1) * mm, "end": v(-3.12, 0.06) * mm});
            skLineSegment(sketch, "E835", {"start": v(-3.12, 0.06) * mm, "end": v(-3.28, -0.01) * mm});
            skLineSegment(sketch, "E836", {"start": v(-3.28, -0.01) * mm, "end": v(-3.44, -0.06) * mm});
            skLineSegment(sketch, "E837", {"start": v(-3.44, -0.06) * mm, "end": v(-3.6, -0.08) * mm});
            skLineSegment(sketch, "E838", {"start": v(-3.6, -0.08) * mm, "end": v(-4.26, -0.08) * mm});
            skLineSegment(sketch, "E839", {"start": v(-4.26, -0.08) * mm, "end": v(-4.26, -1.07) * mm});
            skLineSegment(sketch, "E840", {"start": v(-4.26, -1.07) * mm, "end": v(-4.7, -1.07) * mm});
            skLineSegment(sketch, "E841", {"start": v(-4.7, -1.07) * mm, "end": v(-4.73, -1.1) * mm});
            skLineSegment(sketch, "E842", {"start": v(-4.73, -1.1) * mm, "end": v(-4.74, -1.1) * mm});
            skLineSegment(sketch, "E843", {"start": v(-4.74, -1.1) * mm, "end": v(-4.74, -1.14) * mm});
            skLineSegment(sketch, "E844", {"start": v(-4.74, -1.14) * mm, "end": v(-4.58, -1.14) * mm});
            skLineSegment(sketch, "E845", {"start": v(-4.58, -1.14) * mm, "end": v(-4.58, -1.2) * mm});
            skLineSegment(sketch, "E846", {"start": v(-4.58, -1.2) * mm, "end": v(-4.74, -1.2) * mm});
            skLineSegment(sketch, "E847", {"start": v(-4.74, -1.2) * mm, "end": v(-4.74, -1.28) * mm});
            skLineSegment(sketch, "E848", {"start": v(-4.74, -1.28) * mm, "end": v(-4.65, -1.28) * mm});
            skLineSegment(sketch, "E849", {"start": v(-4.65, -1.28) * mm, "end": v(-4.65, -1.34) * mm});
            skLineSegment(sketch, "E850", {"start": v(-4.65, -1.34) * mm, "end": v(-4.74, -1.34) * mm});
            skLineSegment(sketch, "E851", {"start": v(-4.74, -1.34) * mm, "end": v(-4.74, -1.4) * mm});
            skLineSegment(sketch, "E852", {"start": v(-4.74, -1.4) * mm, "end": v(-4.81, -1.4) * mm});
            skLineSegment(sketch, "E853", {"start": v(-4.81, -1.4) * mm, "end": v(-4.81, -1.34) * mm});
            skLineSegment(sketch, "E854", {"start": v(-4.81, -1.34) * mm, "end": v(-4.9, -1.34) * mm});
            skLineSegment(sketch, "E855", {"start": v(-4.9, -1.34) * mm, "end": v(-4.9, -1.28) * mm});
            skLineSegment(sketch, "E856", {"start": v(-4.9, -1.28) * mm, "end": v(-4.81, -1.28) * mm});
            skLineSegment(sketch, "E857", {"start": v(-4.81, -1.28) * mm, "end": v(-4.81, -1.2) * mm});
            skLineSegment(sketch, "E858", {"start": v(-4.81, -1.2) * mm, "end": v(-4.98, -1.2) * mm});
            skLineSegment(sketch, "E859", {"start": v(-4.98, -1.2) * mm, "end": v(-4.98, -1.14) * mm});
            skLineSegment(sketch, "E860", {"start": v(-4.98, -1.14) * mm, "end": v(-4.81, -1.14) * mm});
            skLineSegment(sketch, "E861", {"start": v(-4.81, -1.14) * mm, "end": v(-4.82, -1.1) * mm});
            skLineSegment(sketch, "E862", {"start": v(-4.82, -1.1) * mm, "end": v(-4.85, -1.1) * mm});
            skLineSegment(sketch, "E863", {"start": v(-4.85, -1.1) * mm, "end": v(-4.86, -1.02) * mm});
            skLineSegment(sketch, "E864", {"start": v(-4.86, -1.02) * mm, "end": v(-4.83, -0.97) * mm});
            skLineSegment(sketch, "E865", {"start": v(-4.83, -0.97) * mm, "end": v(-4.73, -0.97) * mm});
            skLineSegment(sketch, "E866", {"start": v(-4.73, -0.97) * mm, "end": v(-4.71, -0.98) * mm});
            skLineSegment(sketch, "E867", {"start": v(-4.71, -0.98) * mm, "end": v(-4.7, -1) * mm});
            skLineSegment(sketch, "E868", {"start": v(-4.7, -1) * mm, "end": v(-4.33, -1) * mm});
            skLineSegment(sketch, "E869", {"start": v(-4.33, -1) * mm, "end": v(-4.33, 0) * mm});
            skLineSegment(sketch, "E870", {"start": v(-4.33, 0) * mm, "end": v(-3.5, 0) * mm});
            skLineSegment(sketch, "E871", {"start": v(-3.5, 0) * mm, "end": v(-3.3, 0.06) * mm});
            skLineSegment(sketch, "E872", {"start": v(-3.3, 0.06) * mm, "end": v(-3.17, 0.12) * mm});
            skLineSegment(sketch, "E873", {"start": v(-3.17, 0.12) * mm, "end": v(-3.08, 0.19) * mm});
            skLineSegment(sketch, "E874", {"start": v(-3.08, 0.19) * mm, "end": v(-3, 0.25) * mm});
            skLineSegment(sketch, "E875", {"start": v(-3, 0.25) * mm, "end": v(-3, 0.28) * mm});
            skLineSegment(sketch, "E876", {"start": v(-3, 0.28) * mm, "end": v(-2.94, 0.34) * mm});
            skLineSegment(sketch, "E877", {"start": v(-2.94, 0.34) * mm, "end": v(-2.9, 0.43) * mm});
            skLineSegment(sketch, "E878", {"start": v(-2.9, 0.43) * mm, "end": v(-2.87, 0.58) * mm});
            skLineSegment(sketch, "E879", {"start": v(-2.87, 0.58) * mm, "end": v(-2.88, 0.75) * mm});
            skLineSegment(sketch, "E880", {"start": v(-2.88, 0.75) * mm, "end": v(-2.92, 0.88) * mm});
            skLineSegment(sketch, "E881", {"start": v(-2.92, 0.88) * mm, "end": v(-2.98, 1) * mm});
            skLineSegment(sketch, "E882", {"start": v(-2.98, 1) * mm, "end": v(-3.08, 1.1) * mm});
            skLineSegment(sketch, "E883", {"start": v(-3.08, 1.1) * mm, "end": v(-3.21, 1.2) * mm});
            skLineSegment(sketch, "E884", {"start": v(-3.21, 1.2) * mm, "end": v(-3.38, 1.26) * mm});
            skLineSegment(sketch, "E885", {"start": v(-3.38, 1.26) * mm, "end": v(-3.55, 1.3) * mm});
            skLineSegment(sketch, "E886", {"start": v(-3.55, 1.3) * mm, "end": v(-4.75, 1.3) * mm});
            skLineSegment(sketch, "E887", {"start": v(-4.75, 1.3) * mm, "end": v(-4.74, -0.56) * mm});
            skLineSegment(sketch, "E888", {"start": v(-4.74, -0.56) * mm, "end": v(-4.73, -0.56) * mm});
            skLineSegment(sketch, "E889", {"start": v(-4.73, -0.56) * mm, "end": v(-4.71, -0.57) * mm});
            skLineSegment(sketch, "E890", {"start": v(-4.71, -0.57) * mm, "end": v(-4.7, -0.6) * mm});
            skLineSegment(sketch, "E891", {"start": v(-4.7, -0.6) * mm, "end": v(-4.7, -0.68) * mm});
            skLineSegment(sketch, "E892", {"start": v(-4.7, -0.68) * mm, "end": v(-4.74, -0.7) * mm});
            skLineSegment(sketch, "E893", {"start": v(-4.74, -0.7) * mm, "end": v(-4.82, -0.7) * mm});
            skLineSegment(sketch, "E894", {"start": v(-4.82, -0.7) * mm, "end": v(-4.85, -0.69) * mm});
            skLineSegment(sketch, "E895", {"start": v(-4.85, -0.69) * mm, "end": v(-4.86, -0.6) * mm});
            skLineSegment(sketch, "E896", {"start": v(-4.86, -0.6) * mm, "end": v(-4.84, -0.56) * mm});
            skLineSegment(sketch, "E897", {"start": v(-4.84, -0.56) * mm, "end": v(-4.82, -0.56) * mm});
            skLineSegment(sketch, "E898", {"start": v(-4.82, -0.56) * mm, "end": v(-4.82, 1.37) * mm});
            skLineSegment(sketch, "E899", {"start": v(-4.82, 1.37) * mm, "end": v(-3.6, 1.37) * mm});
            skLineSegment(sketch, "E900", {"start": v(-4.74, 1.64) * mm, "end": v(-4.71, 1.62) * mm});
            skLineSegment(sketch, "E901", {"start": v(-4.71, 1.62) * mm, "end": v(-4.7, 1.6) * mm});
            skLineSegment(sketch, "E902", {"start": v(-4.7, 1.6) * mm, "end": v(-3.52, 1.6) * mm});
            skLineSegment(sketch, "E903", {"start": v(-3.52, 1.6) * mm, "end": v(-3.27, 1.55) * mm});
            skLineSegment(sketch, "E904", {"start": v(-3.27, 1.55) * mm, "end": v(-3.08, 1.48) * mm});
            skLineSegment(sketch, "E905", {"start": v(-3.08, 1.48) * mm, "end": v(-2.94, 1.4) * mm});
            skLineSegment(sketch, "E906", {"start": v(-2.94, 1.4) * mm, "end": v(-2.82, 1.3) * mm});
            skLineSegment(sketch, "E907", {"start": v(-2.82, 1.3) * mm, "end": v(-2.77, 1.25) * mm});
            skLineSegment(sketch, "E908", {"start": v(-2.77, 1.25) * mm, "end": v(-2.75, 1.22) * mm});
            skLineSegment(sketch, "E909", {"start": v(-2.75, 1.22) * mm, "end": v(-2.74, 1.22) * mm});
            skLineSegment(sketch, "E910", {"start": v(-2.74, 1.22) * mm, "end": v(-2.66, 1.09) * mm});
            skLineSegment(sketch, "E911", {"start": v(-2.66, 1.09) * mm, "end": v(-2.6, 0.94) * mm});
            skLineSegment(sketch, "E912", {"start": v(-2.6, 0.94) * mm, "end": v(-2.57, 0.8) * mm});
            skLineSegment(sketch, "E913", {"start": v(-2.57, 0.8) * mm, "end": v(-2.57, 0.47) * mm});
            skLineSegment(sketch, "E914", {"start": v(-2.57, 0.47) * mm, "end": v(-2.61, 0.28) * mm});
            skLineSegment(sketch, "E915", {"start": v(-2.61, 0.28) * mm, "end": v(-2.67, 0.15) * mm});
            skLineSegment(sketch, "E916", {"start": v(-2.67, 0.15) * mm, "end": v(-2.73, 0.06) * mm});
            skLineSegment(sketch, "E917", {"start": v(-2.73, 0.06) * mm, "end": v(-2.85, -0.07) * mm});
            skLineSegment(sketch, "E918", {"start": v(-2.85, -0.07) * mm, "end": v(-2.89, -0.1) * mm});
            skLineSegment(sketch, "E919", {"start": v(-2.89, -0.1) * mm, "end": v(-2.96, -0.16) * mm});
            skLineSegment(sketch, "E920", {"start": v(-2.96, -0.16) * mm, "end": v(-3.11, -0.24) * mm});
            skLineSegment(sketch, "E921", {"start": v(-3.11, -0.24) * mm, "end": v(-3.29, -0.3) * mm});
            skLineSegment(sketch, "E922", {"start": v(-3.29, -0.3) * mm, "end": v(-3.48, -0.34) * mm});
            skLineSegment(sketch, "E923", {"start": v(-3.48, -0.34) * mm, "end": v(-4.02, -0.34) * mm});
            skLineSegment(sketch, "E924", {"start": v(-4.02, -0.34) * mm, "end": v(-4.02, -0.97) * mm});
            skLineSegment(sketch, "E925", {"start": v(-4.02, -0.97) * mm, "end": v(-4, -0.97) * mm});
            skLineSegment(sketch, "E926", {"start": v(-4, -0.97) * mm, "end": v(-3.98, -1.01) * mm});
            skLineSegment(sketch, "E927", {"start": v(-3.98, -1.01) * mm, "end": v(-4, -1.08) * mm});
            skLineSegment(sketch, "E928", {"start": v(-4, -1.08) * mm, "end": v(-4.02, -1.1) * mm});
            skLineSegment(sketch, "E929", {"start": v(-4.02, -1.1) * mm, "end": v(-4.08, -1.13) * mm});
            skLineSegment(sketch, "E930", {"start": v(-4.08, -1.13) * mm, "end": v(-4.14, -1.1) * mm});
            skLineSegment(sketch, "E931", {"start": v(-4.14, -1.1) * mm, "end": v(-4.15, -1.06) * mm});
            skLineSegment(sketch, "E932", {"start": v(-4.15, -1.06) * mm, "end": v(-4.14, -1) * mm});
            skLineSegment(sketch, "E933", {"start": v(-4.14, -1) * mm, "end": v(-4.1, -0.96) * mm});
            skLineSegment(sketch, "E934", {"start": v(-4.1, -0.96) * mm, "end": v(-4.1, -0.27) * mm});
            skLineSegment(sketch, "E935", {"start": v(-4.1, -0.27) * mm, "end": v(-3.45, -0.26) * mm});
            skLineSegment(sketch, "E936", {"start": v(-3.45, -0.26) * mm, "end": v(-3.27, -0.22) * mm});
            skLineSegment(sketch, "E937", {"start": v(-3.27, -0.22) * mm, "end": v(-3.1, -0.15) * mm});
            skLineSegment(sketch, "E938", {"start": v(-3.1, -0.15) * mm, "end": v(-2.95, -0.06) * mm});
            skLineSegment(sketch, "E939", {"start": v(-2.95, -0.06) * mm, "end": v(-2.83, 0.06) * mm});
            skLineSegment(sketch, "E940", {"start": v(-2.83, 0.06) * mm, "end": v(-2.81, 0.09) * mm});
            skLineSegment(sketch, "E941", {"start": v(-2.81, 0.09) * mm, "end": v(-2.76, 0.15) * mm});
            skLineSegment(sketch, "E942", {"start": v(-2.76, 0.15) * mm, "end": v(-2.74, 0.19) * mm});
            skLineSegment(sketch, "E943", {"start": v(-2.74, 0.19) * mm, "end": v(-2.7, 0.25) * mm});
            skLineSegment(sketch, "E944", {"start": v(-2.7, 0.25) * mm, "end": v(-2.65, 0.4) * mm});
            skLineSegment(sketch, "E945", {"start": v(-2.65, 0.4) * mm, "end": v(-2.63, 0.67) * mm});
            skLineSegment(sketch, "E946", {"start": v(-2.63, 0.67) * mm, "end": v(-2.66, 0.88) * mm});
            skLineSegment(sketch, "E947", {"start": v(-2.66, 0.88) * mm, "end": v(-2.72, 1.05) * mm});
            skLineSegment(sketch, "E948", {"start": v(-2.72, 1.05) * mm, "end": v(-2.8, 1.18) * mm});
            skLineSegment(sketch, "E949", {"start": v(-2.8, 1.18) * mm, "end": v(-2.9, 1.28) * mm});
            skLineSegment(sketch, "E950", {"start": v(-2.9, 1.28) * mm, "end": v(-2.94, 1.3) * mm});
            skLineSegment(sketch, "E951", {"start": v(-2.94, 1.3) * mm, "end": v(-3.02, 1.37) * mm});
            skLineSegment(sketch, "E952", {"start": v(-3.02, 1.37) * mm, "end": v(-3.12, 1.42) * mm});
            skLineSegment(sketch, "E953", {"start": v(-3.12, 1.42) * mm, "end": v(-3.3, 1.48) * mm});
            skLineSegment(sketch, "E954", {"start": v(-3.3, 1.48) * mm, "end": v(-3.48, 1.52) * mm});
            skLineSegment(sketch, "E955", {"start": v(-3.48, 1.52) * mm, "end": v(-4.71, 1.52) * mm});
            skLineSegment(sketch, "E956", {"start": v(-4.71, 1.52) * mm, "end": v(-4.73, 1.49) * mm});
            skLineSegment(sketch, "E957", {"start": v(-4.73, 1.49) * mm, "end": v(-4.83, 1.49) * mm});
            skLineSegment(sketch, "E958", {"start": v(-4.83, 1.49) * mm, "end": v(-4.86, 1.52) * mm});
            skLineSegment(sketch, "E959", {"start": v(-4.86, 1.52) * mm, "end": v(-4.86, 1.6) * mm});
            skLineSegment(sketch, "E960", {"start": v(-4.86, 1.6) * mm, "end": v(-4.82, 1.64) * mm});
            skLineSegment(sketch, "E961", {"start": v(-4.82, 1.64) * mm, "end": v(-4.74, 1.64) * mm});
            skLineSegment(sketch, "E962", {"start": v(-1.31, 1.54) * mm, "end": v(-1.2, 1.53) * mm});
            skLineSegment(sketch, "E963", {"start": v(-1.2, 1.53) * mm, "end": v(-2.45, 0.28) * mm});
            skLineSegment(sketch, "E964", {"start": v(-2.45, 0.28) * mm, "end": v(-2.47, 1.54) * mm});
            skLineSegment(sketch, "E965", {"start": v(-2.47, 1.54) * mm, "end": v(-1.31, 1.54) * mm});
            skLineSegment(sketch, "E966", {"start": v(2.33, 1.54) * mm, "end": v(2.25, 1.54) * mm});
            skLineSegment(sketch, "E967", {"start": v(2.25, 1.54) * mm, "end": v(2.43, -0.9) * mm});
            skLineSegment(sketch, "E968", {"start": v(2.43, -0.9) * mm, "end": v(2.46, -0.9) * mm});
            skLineSegment(sketch, "E969", {"start": v(2.46, -0.9) * mm, "end": v(3.39, -0.95) * mm});
            skLineSegment(sketch, "E970", {"start": v(3.39, -0.95) * mm, "end": v(3.6, -0.92) * mm});
            skLineSegment(sketch, "E971", {"start": v(3.6, -0.92) * mm, "end": v(3.77, -0.87) * mm});
            skLineSegment(sketch, "E972", {"start": v(3.77, -0.87) * mm, "end": v(3.92, -0.8) * mm});
            skLineSegment(sketch, "E973", {"start": v(3.92, -0.8) * mm, "end": v(4.03, -0.72) * mm});
            skLineSegment(sketch, "E974", {"start": v(4.03, -0.72) * mm, "end": v(4.14, -0.62) * mm});
            skLineSegment(sketch, "E975", {"start": v(4.14, -0.62) * mm, "end": v(4.15, -0.59) * mm});
            skLineSegment(sketch, "E976", {"start": v(4.15, -0.59) * mm, "end": v(4.2, -0.53) * mm});
            skLineSegment(sketch, "E977", {"start": v(4.2, -0.53) * mm, "end": v(4.22, -0.49) * mm});
            skLineSegment(sketch, "E978", {"start": v(4.22, -0.49) * mm, "end": v(4.27, -0.4) * mm});
            skLineSegment(sketch, "E979", {"start": v(4.27, -0.4) * mm, "end": v(4.33, -0.2) * mm});
            skLineSegment(sketch, "E980", {"start": v(4.33, -0.2) * mm, "end": v(4.36, -0.04) * mm});
            skLineSegment(sketch, "E981", {"start": v(4.36, -0.04) * mm, "end": v(4.35, 0.3) * mm});
            skLineSegment(sketch, "E982", {"start": v(4.35, 0.3) * mm, "end": v(4.3, 0.54) * mm});
            skLineSegment(sketch, "E983", {"start": v(4.3, 0.54) * mm, "end": v(4.22, 0.77) * mm});
            skLineSegment(sketch, "E984", {"start": v(4.22, 0.77) * mm, "end": v(4.11, 0.95) * mm});
            skLineSegment(sketch, "E985", {"start": v(4.11, 0.95) * mm, "end": v(4.05, 1.03) * mm});
            skLineSegment(sketch, "E986", {"start": v(4.05, 1.03) * mm, "end": v(4.03, 1.06) * mm});
            skLineSegment(sketch, "E987", {"start": v(4.03, 1.06) * mm, "end": v(3.92, 1.17) * mm});
            skLineSegment(sketch, "E988", {"start": v(3.92, 1.17) * mm, "end": v(3.88, 1.2) * mm});
            skLineSegment(sketch, "E989", {"start": v(3.88, 1.2) * mm, "end": v(3.82, 1.25) * mm});
            skLineSegment(sketch, "E990", {"start": v(3.82, 1.25) * mm, "end": v(3.65, 1.34) * mm});
            skLineSegment(sketch, "E991", {"start": v(3.65, 1.34) * mm, "end": v(3.48, 1.42) * mm});
            skLineSegment(sketch, "E992", {"start": v(3.48, 1.42) * mm, "end": v(3.26, 1.48) * mm});
            skLineSegment(sketch, "E993", {"start": v(3.26, 1.48) * mm, "end": v(3.12, 1.5) * mm});
            skLineSegment(sketch, "E994", {"start": v(3.12, 1.5) * mm, "end": v(2.33, 1.54) * mm});
            skLineSegment(sketch, "E995", {"start": v(2.83, 1.78) * mm, "end": v(3.68, 1.74) * mm});
            skLineSegment(sketch, "E996", {"start": v(3.68, 1.74) * mm, "end": v(3.9, 1.67) * mm});
            skLineSegment(sketch, "E997", {"start": v(3.9, 1.67) * mm, "end": v(4.14, 1.56) * mm});
            skLineSegment(sketch, "E998", {"start": v(4.14, 1.56) * mm, "end": v(4.3, 1.46) * mm});
            skLineSegment(sketch, "E999", {"start": v(4.3, 1.46) * mm, "end": v(4.37, 1.4) * mm});
            skLineSegment(sketch, "E1000", {"start": v(4.37, 1.4) * mm, "end": v(4.39, 1.4) * mm});
            skLineSegment(sketch, "E1001", {"start": v(4.39, 1.4) * mm, "end": v(4.55, 1.23) * mm});
            skLineSegment(sketch, "E1002", {"start": v(4.55, 1.23) * mm, "end": v(4.56, 1.2) * mm});
            skLineSegment(sketch, "E1003", {"start": v(4.56, 1.2) * mm, "end": v(4.57, 1.2) * mm});
            skLineSegment(sketch, "E1004", {"start": v(4.57, 1.2) * mm, "end": v(4.67, 1.05) * mm});
            skLineSegment(sketch, "E1005", {"start": v(4.67, 1.05) * mm, "end": v(4.69, 1.01) * mm});
            skLineSegment(sketch, "E1006", {"start": v(4.69, 1.01) * mm, "end": v(4.7, 1.01) * mm});
            skLineSegment(sketch, "E1007", {"start": v(4.7, 1.01) * mm, "end": v(4.77, 0.84) * mm});
            skLineSegment(sketch, "E1008", {"start": v(4.77, 0.84) * mm, "end": v(4.83, 0.68) * mm});
            skLineSegment(sketch, "E1009", {"start": v(4.83, 0.68) * mm, "end": v(4.86, 0.51) * mm});
            skLineSegment(sketch, "E1010", {"start": v(4.86, 0.51) * mm, "end": v(4.86, 0.12) * mm});
            skLineSegment(sketch, "E1011", {"start": v(4.86, 0.12) * mm, "end": v(4.8, -0.07) * mm});
            skLineSegment(sketch, "E1012", {"start": v(4.8, -0.07) * mm, "end": v(4.75, -0.19) * mm});
            skLineSegment(sketch, "E1013", {"start": v(4.75, -0.19) * mm, "end": v(4.65, -0.34) * mm});
            skLineSegment(sketch, "E1014", {"start": v(4.65, -0.34) * mm, "end": v(4.6, -0.4) * mm});
            skLineSegment(sketch, "E1015", {"start": v(4.6, -0.4) * mm, "end": v(4.58, -0.42) * mm});
            skLineSegment(sketch, "E1016", {"start": v(4.58, -0.42) * mm, "end": v(4.48, -0.52) * mm});
            skLineSegment(sketch, "E1017", {"start": v(4.48, -0.52) * mm, "end": v(4.45, -0.54) * mm});
            skLineSegment(sketch, "E1018", {"start": v(4.45, -0.54) * mm, "end": v(4.4, -0.59) * mm});
            skLineSegment(sketch, "E1019", {"start": v(4.4, -0.59) * mm, "end": v(4.26, -0.69) * mm});
            skLineSegment(sketch, "E1020", {"start": v(4.26, -0.69) * mm, "end": v(4.14, -0.75) * mm});
            skLineSegment(sketch, "E1021", {"start": v(4.14, -0.75) * mm, "end": v(4.02, -0.81) * mm});
            skLineSegment(sketch, "E1022", {"start": v(4.02, -0.81) * mm, "end": v(4, -0.84) * mm});
            skLineSegment(sketch, "E1023", {"start": v(4, -0.84) * mm, "end": v(3.86, -0.91) * mm});
            skLineSegment(sketch, "E1024", {"start": v(3.86, -0.91) * mm, "end": v(3.66, -0.98) * mm});
            skLineSegment(sketch, "E1025", {"start": v(3.66, -0.98) * mm, "end": v(3.43, -1.02) * mm});
            skLineSegment(sketch, "E1026", {"start": v(3.43, -1.02) * mm, "end": v(3.1, -1.01) * mm});
            skLineSegment(sketch, "E1027", {"start": v(3.1, -1.01) * mm, "end": v(2.37, -0.96) * mm});
            skLineSegment(sketch, "E1028", {"start": v(2.37, -0.96) * mm, "end": v(2.32, -0.36) * mm});
            skLineSegment(sketch, "E1029", {"start": v(2.32, -0.36) * mm, "end": v(2.23, -0.47) * mm});
            skLineSegment(sketch, "E1030", {"start": v(2.23, -0.47) * mm, "end": v(2.21, -0.5) * mm});
            skLineSegment(sketch, "E1031", {"start": v(2.21, -0.5) * mm, "end": v(2.17, -0.52) * mm});
            skLineSegment(sketch, "E1032", {"start": v(2.17, -0.52) * mm, "end": v(2.16, -0.54) * mm});
            skLineSegment(sketch, "E1033", {"start": v(2.16, -0.54) * mm, "end": v(2, -0.63) * mm});
            skLineSegment(sketch, "E1034", {"start": v(2, -0.63) * mm, "end": v(1.9, -0.66) * mm});
            skLineSegment(sketch, "E1035", {"start": v(1.9, -0.66) * mm, "end": v(1.5, -0.84) * mm});
            skLineSegment(sketch, "E1036", {"start": v(1.5, -0.84) * mm, "end": v(1.36, -0.9) * mm});
            skLineSegment(sketch, "E1037", {"start": v(1.36, -0.9) * mm, "end": v(1.2, -0.92) * mm});
            skLineSegment(sketch, "E1038", {"start": v(1.2, -0.92) * mm, "end": v(0.94, -0.91) * mm});
            skLineSegment(sketch, "E1039", {"start": v(0.94, -0.91) * mm, "end": v(0.75, -0.87) * mm});
            skLineSegment(sketch, "E1040", {"start": v(0.75, -0.87) * mm, "end": v(0.52, -0.78) * mm});
            skLineSegment(sketch, "E1041", {"start": v(0.52, -0.78) * mm, "end": v(0.36, -0.67) * mm});
            skLineSegment(sketch, "E1042", {"start": v(0.36, -0.67) * mm, "end": v(0.28, -0.6) * mm});
            skLineSegment(sketch, "E1043", {"start": v(0.28, -0.6) * mm, "end": v(0.24, -0.58) * mm});
            skLineSegment(sketch, "E1044", {"start": v(0.24, -0.58) * mm, "end": v(0.17, -0.5) * mm});
            skLineSegment(sketch, "E1045", {"start": v(0.17, -0.5) * mm, "end": v(0.15, -0.47) * mm});
            skLineSegment(sketch, "E1046", {"start": v(0.15, -0.47) * mm, "end": v(0.11, -0.44) * mm});
            skLineSegment(sketch, "E1047", {"start": v(0.11, -0.44) * mm, "end": v(0.13, -0.4) * mm});
            skLineSegment(sketch, "E1048", {"start": v(0.13, -0.4) * mm, "end": v(0.16, -0.37) * mm});
            skLineSegment(sketch, "E1049", {"start": v(0.16, -0.37) * mm, "end": v(0.18, -0.33) * mm});
            skLineSegment(sketch, "E1050", {"start": v(0.18, -0.33) * mm, "end": v(0.23, -0.28) * mm});
            skLineSegment(sketch, "E1051", {"start": v(0.23, -0.28) * mm, "end": v(0.26, -0.24) * mm});
            skLineSegment(sketch, "E1052", {"start": v(0.26, -0.24) * mm, "end": v(0.31, -0.19) * mm});
            skLineSegment(sketch, "E1053", {"start": v(0.31, -0.19) * mm, "end": v(0.33, -0.15) * mm});
            skLineSegment(sketch, "E1054", {"start": v(0.33, -0.15) * mm, "end": v(0.39, -0.1) * mm});
            skLineSegment(sketch, "E1055", {"start": v(0.39, -0.1) * mm, "end": v(0.4, -0.06) * mm});
            skLineSegment(sketch, "E1056", {"start": v(0.4, -0.06) * mm, "end": v(0.46, 0) * mm});
            skLineSegment(sketch, "E1057", {"start": v(0.46, 0) * mm, "end": v(0.98, 0.15) * mm});
            skLineSegment(sketch, "E1058", {"start": v(0.98, 0.15) * mm, "end": v(1.02, 0.15) * mm});
            skLineSegment(sketch, "E1059", {"start": v(1.02, 0.15) * mm, "end": v(1.11, 0.05) * mm});
            skLineSegment(sketch, "E1060", {"start": v(1.11, 0.05) * mm, "end": v(1.13, 0.05) * mm});
            skLineSegment(sketch, "E1061", {"start": v(1.13, 0.05) * mm, "end": v(1.15, 0.02) * mm});
            skLineSegment(sketch, "E1062", {"start": v(1.15, 0.02) * mm, "end": v(1.17, 0.02) * mm});
            skLineSegment(sketch, "E1063", {"start": v(1.17, 0.02) * mm, "end": v(1.18, 0) * mm});
            skLineSegment(sketch, "E1064", {"start": v(1.18, 0) * mm, "end": v(1.2, 0) * mm});
            skLineSegment(sketch, "E1065", {"start": v(1.2, 0) * mm, "end": v(1.21, -0.03) * mm});
            skLineSegment(sketch, "E1066", {"start": v(1.21, -0.03) * mm, "end": v(1.23, -0.03) * mm});
            skLineSegment(sketch, "E1067", {"start": v(1.23, -0.03) * mm, "end": v(1.25, -0.04) * mm});
            skLineSegment(sketch, "E1068", {"start": v(1.25, -0.04) * mm, "end": v(1.23, 0.03) * mm});
            skLineSegment(sketch, "E1069", {"start": v(1.23, 0.03) * mm, "end": v(1.17, 0.1) * mm});
            skLineSegment(sketch, "E1070", {"start": v(1.17, 0.1) * mm, "end": v(1.07, 0.15) * mm});
            skLineSegment(sketch, "E1071", {"start": v(1.07, 0.15) * mm, "end": v(0.9, 0.2) * mm});
            skLineSegment(sketch, "E1072", {"start": v(0.9, 0.2) * mm, "end": v(0.74, 0.22) * mm});
            skLineSegment(sketch, "E1073", {"start": v(0.74, 0.22) * mm, "end": v(0.63, 0.22) * mm});
            skLineSegment(sketch, "E1074", {"start": v(0.63, 0.22) * mm, "end": v(0.52, 0.55) * mm});
            skLineSegment(sketch, "E1075", {"start": v(0.52, 0.55) * mm, "end": v(0.5, 0.59) * mm});
            skLineSegment(sketch, "E1076", {"start": v(0.5, 0.59) * mm, "end": v(0.58, 0.66) * mm});
            skLineSegment(sketch, "E1077", {"start": v(0.58, 0.66) * mm, "end": v(0.6, 0.69) * mm});
            skLineSegment(sketch, "E1078", {"start": v(0.6, 0.69) * mm, "end": v(0.67, 0.75) * mm});
            skLineSegment(sketch, "E1079", {"start": v(0.67, 0.75) * mm, "end": v(0.7, 0.8) * mm});
            skLineSegment(sketch, "E1080", {"start": v(0.7, 0.8) * mm, "end": v(0.77, 0.85) * mm});
            skLineSegment(sketch, "E1081", {"start": v(0.77, 0.85) * mm, "end": v(0.78, 0.88) * mm});
            skLineSegment(sketch, "E1082", {"start": v(0.78, 0.88) * mm, "end": v(0.89, 0.9) * mm});
            skLineSegment(sketch, "E1083", {"start": v(0.89, 0.9) * mm, "end": v(1.32, 1.04) * mm});
            skLineSegment(sketch, "E1084", {"start": v(1.32, 1.04) * mm, "end": v(1.4, 1.04) * mm});
            skLineSegment(sketch, "E1085", {"start": v(1.4, 1.04) * mm, "end": v(1.92, 1) * mm});
            skLineSegment(sketch, "E1086", {"start": v(1.92, 1) * mm, "end": v(1.86, 0.92) * mm});
            skLineSegment(sketch, "E1087", {"start": v(1.86, 0.92) * mm, "end": v(1.74, 0.8) * mm});
            skLineSegment(sketch, "E1088", {"start": v(1.74, 0.8) * mm, "end": v(1.75, 0.8) * mm});
            skLineSegment(sketch, "E1089", {"start": v(1.75, 0.8) * mm, "end": v(1.97, 0.7) * mm});
            skLineSegment(sketch, "E1090", {"start": v(1.97, 0.7) * mm, "end": v(2.12, 0.6) * mm});
            skLineSegment(sketch, "E1091", {"start": v(2.12, 0.6) * mm, "end": v(2.25, 0.49) * mm});
            skLineSegment(sketch, "E1092", {"start": v(2.25, 0.49) * mm, "end": v(2.26, 0.47) * mm});
            skLineSegment(sketch, "E1093", {"start": v(2.26, 0.47) * mm, "end": v(2.17, 1.62) * mm});
            skLineSegment(sketch, "E1094", {"start": v(2.17, 1.62) * mm, "end": v(2.23, 1.62) * mm});
            skLineSegment(sketch, "E1095", {"start": v(2.23, 1.62) * mm, "end": v(2.44, 1.7) * mm});
            skLineSegment(sketch, "E1096", {"start": v(2.44, 1.7) * mm, "end": v(2.64, 1.78) * mm});
            skLineSegment(sketch, "E1097", {"start": v(2.64, 1.78) * mm, "end": v(2.83, 1.78) * mm});
            skLineSegment(sketch, "E1098", {"start": v(1.63, 1.83) * mm, "end": v(1.63, 1.73) * mm});
            skLineSegment(sketch, "E1099", {"start": v(1.63, 1.73) * mm, "end": v(2.04, 1.73) * mm});
            skLineSegment(sketch, "E1100", {"start": v(2.04, 1.73) * mm, "end": v(2.04, 1.62) * mm});
            skLineSegment(sketch, "E1101", {"start": v(2.04, 1.62) * mm, "end": v(1.63, 1.62) * mm});
            skLineSegment(sketch, "E1102", {"start": v(1.63, 1.62) * mm, "end": v(1.63, 1.53) * mm});
            skLineSegment(sketch, "E1103", {"start": v(1.63, 1.53) * mm, "end": v(2.04, 1.53) * mm});
            skLineSegment(sketch, "E1104", {"start": v(2.04, 1.53) * mm, "end": v(2.04, 1.43) * mm});
            skLineSegment(sketch, "E1105", {"start": v(2.04, 1.43) * mm, "end": v(1.63, 1.43) * mm});
            skLineSegment(sketch, "E1106", {"start": v(1.63, 1.43) * mm, "end": v(1.62, 1.4) * mm});
            skLineSegment(sketch, "E1107", {"start": v(1.62, 1.4) * mm, "end": v(1.44, 1.22) * mm});
            skLineSegment(sketch, "E1108", {"start": v(1.44, 1.22) * mm, "end": v(1.31, 1.22) * mm});
            skLineSegment(sketch, "E1109", {"start": v(1.31, 1.22) * mm, "end": v(1.27, 1.28) * mm});
            skLineSegment(sketch, "E1110", {"start": v(1.27, 1.28) * mm, "end": v(1.23, 1.3) * mm});
            skLineSegment(sketch, "E1111", {"start": v(1.23, 1.3) * mm, "end": v(1.13, 1.4) * mm});
            skLineSegment(sketch, "E1112", {"start": v(1.13, 1.4) * mm, "end": v(1.13, 1.43) * mm});
            skLineSegment(sketch, "E1113", {"start": v(1.13, 1.43) * mm, "end": v(-0.17, 1.43) * mm});
            skLineSegment(sketch, "E1114", {"start": v(-0.17, 1.43) * mm, "end": v(-0.17, 1.53) * mm});
            skLineSegment(sketch, "E1115", {"start": v(-0.17, 1.53) * mm, "end": v(1.13, 1.53) * mm});
            skLineSegment(sketch, "E1116", {"start": v(1.13, 1.53) * mm, "end": v(1.13, 1.62) * mm});
            skLineSegment(sketch, "E1117", {"start": v(1.13, 1.62) * mm, "end": v(-0.17, 1.62) * mm});
            skLineSegment(sketch, "E1118", {"start": v(-0.17, 1.62) * mm, "end": v(-0.17, 1.73) * mm});
            skLineSegment(sketch, "E1119", {"start": v(-0.17, 1.73) * mm, "end": v(1.13, 1.73) * mm});
            skLineSegment(sketch, "E1120", {"start": v(1.13, 1.73) * mm, "end": v(1.13, 1.83) * mm});
            skLineSegment(sketch, "E1121", {"start": v(1.13, 1.83) * mm, "end": v(1.63, 1.83) * mm});
            skLineSegment(sketch, "E1122.bottom", {"start": v(-5.73, 2.22) * mm, "end": v(5.67, 2.22) * mm});
            skLineSegment(sketch, "E1122.top", {"start": v(-5.73, -2.25) * mm, "end": v(5.67, -2.25) * mm});
            skLineSegment(sketch, "E1122.left", {"start": v(-5.73, 2.22) * mm, "end": v(-5.73, -2.25) * mm});
            skLineSegment(sketch, "E1122.right", {"start": v(5.67, 2.22) * mm, "end": v(5.67, -2.25) * mm});
            skLineSegment(sketch, "E1123", {"start": v(1.08, 0.9) * mm, "end": v(1.45, 0.86) * mm});
            skLineSegment(sketch, "E1124", {"start": v(1.45, 0.86) * mm, "end": v(1.73, 0.97) * mm});
            skLineSegment(sketch, "E1125", {"start": v(1.08, 0.9) * mm, "end": v(1.35, 1) * mm});
            skLineSegment(sketch, "E1126", {"start": v(1.35, 1) * mm, "end": v(1.73, 0.97) * mm});
            skPoint(sketch, "E1127", {"position": v(1.08, 0.8) * mm});
            skSolve(sketch);
        }
        {
            var Q0;
            Q0=makeQuery(id+"F0.imprint","IMPRINT",FACE,{"disambiguationData":[TD([[makeQuery(id+"F0.imprint","IMPRINT",EDGE,{"derivedFrom":sQuery(id+"F0.wireOp",EDGE,"E805")}),-1.0]])]});
            var Q1;
            Q1=makeQuery(id+"F0.imprint","IMPRINT",FACE,{"disambiguationData":[TD([[makeQuery(id+"F0.imprint","IMPRINT",EDGE,{"derivedFrom":sQuery(id+"F0.wireOp",EDGE,"E900")}),-1.0]])]});
            var Q2;
            Q2=makeQuery(id+"F0.imprint","IMPRINT",FACE,{"disambiguationData":[TD([[makeQuery(id+"F0.imprint","IMPRINT",EDGE,{"derivedFrom":sQuery(id+"F0.wireOp",EDGE,"E190")}),-1.0]])]});
            var Q3;
            Q3=makeQuery(id+"F0.imprint","IMPRINT",FACE,{"disambiguationData":[TD([[makeQuery(id+"F0.imprint","IMPRINT",EDGE,{"derivedFrom":sQuery(id+"F0.wireOp",EDGE,"E610")}),-1.0]])]});
            var Q4;
            Q4=makeQuery(id+"F0.imprint","IMPRINT",FACE,{"disambiguationData":[TD([[makeQuery(id+"F0.imprint","IMPRINT",EDGE,{"derivedFrom":sQuery(id+"F0.wireOp",EDGE,"E711")}),1.0]])]});
            var Q5;
            Q5=makeQuery(id+"F0.imprint","IMPRINT",FACE,{"disambiguationData":[TD([[makeQuery(id+"F0.imprint","IMPRINT",EDGE,{"derivedFrom":sQuery(id+"F0.wireOp",EDGE,"E407")}),-1.0]])]});
            var Q6;
            Q6=makeQuery(id+"F0.imprint","IMPRINT",FACE,{"disambiguationData":[TD([[makeQuery(id+"F0.imprint","IMPRINT",EDGE,{"derivedFrom":sQuery(id+"F0.wireOp",EDGE,"E594")}),-1.0]])]});
            var Q7;
            Q7=makeQuery(id+"F0.imprint","IMPRINT",FACE,{"disambiguationData":[TD([[makeQuery(id+"F0.imprint","IMPRINT",EDGE,{"derivedFrom":sQuery(id+"F0.wireOp",EDGE,"E699")}),-1.0]])]});
            var Q8;
            Q8=makeQuery(id+"F0.imprint","IMPRINT",FACE,{"disambiguationData":[TD([[makeQuery(id+"F0.imprint","IMPRINT",EDGE,{"derivedFrom":sQuery(id+"F0.wireOp",EDGE,"E291")}),-1.0]])]});
            var Q9;
            Q9=makeQuery(id+"F0.imprint","IMPRINT",FACE,{"disambiguationData":[TD([[makeQuery(id+"F0.imprint","IMPRINT",EDGE,{"derivedFrom":sQuery(id+"F0.wireOp",EDGE,"E590")}),-1.0]])]});
            var Q10;
            Q10=makeQuery(id+"F0.imprint","IMPRINT",FACE,{"disambiguationData":[TD([[makeQuery(id+"F0.imprint","IMPRINT",EDGE,{"derivedFrom":sQuery(id+"F0.wireOp",EDGE,"E257")}),-1.0]])]});
            var Q11;
            Q11=makeQuery(id+"F0.imprint","IMPRINT",FACE,{"disambiguationData":[TD([[makeQuery(id+"F0.imprint","IMPRINT",EDGE,{"derivedFrom":sQuery(id+"F0.wireOp",EDGE,"E559")}),-1.0]])]});
            var Q12;
            Q12=makeQuery(id+"F0.imprint","IMPRINT",FACE,{"disambiguationData":[TD([[makeQuery(id+"F0.imprint","IMPRINT",EDGE,{"derivedFrom":sQuery(id+"F0.wireOp",EDGE,"E1123")}),1.0]])]});
            var Q13;
            Q13=makeQuery(id+"F0.imprint","IMPRINT",FACE,{"disambiguationData":[TD([[makeQuery(id+"F0.imprint","IMPRINT",EDGE,{"derivedFrom":sQuery(id+"F0.wireOp",EDGE,"E157")}),-1.0]])]});
            var Q14;
            Q14=makeQuery(id+"F0.imprint","IMPRINT",FACE,{"disambiguationData":[TD([[makeQuery(id+"F0.imprint","IMPRINT",EDGE,{"derivedFrom":sQuery(id+"F0.wireOp",EDGE,"E217")}),-1.0]])]});
            var Q15;
            Q15=makeQuery(id+"F0.imprint","IMPRINT",FACE,{"disambiguationData":[TD([[makeQuery(id+"F0.imprint","IMPRINT",EDGE,{"derivedFrom":sQuery(id+"F0.wireOp",EDGE,"E787")}),-1.0]])]});
            var Q16;
            Q16=makeQuery(id+"F0.imprint","IMPRINT",FACE,{"disambiguationData":[TD([[makeQuery(id+"F0.imprint","IMPRINT",EDGE,{"derivedFrom":sQuery(id+"F0.wireOp",EDGE,"E202")}),-1.0]])]});
            var Q17;
            Q17=makeQuery(id+"F0.imprint","IMPRINT",FACE,{"disambiguationData":[TD([[makeQuery(id+"F0.imprint","IMPRINT",EDGE,{"derivedFrom":sQuery(id+"F0.wireOp",EDGE,"E505")}),-1.0]])]});
            var Q18;
            Q18=makeQuery(id+"F0.imprint","IMPRINT",FACE,{"disambiguationData":[TD([[makeQuery(id+"F0.imprint","IMPRINT",EDGE,{"derivedFrom":sQuery(id+"F0.wireOp",EDGE,"E729")}),1.0]])]});
            var Q19;
            Q19=makeQuery(id+"F0.imprint","IMPRINT",FACE,{"disambiguationData":[TD([[makeQuery(id+"F0.imprint","IMPRINT",EDGE,{"derivedFrom":sQuery(id+"F0.wireOp",EDGE,"E699")}),1.0]])]});
            var Q20;
            Q20=makeQuery(id+"F0.imprint","IMPRINT",FACE,{"disambiguationData":[TD([[makeQuery(id+"F0.imprint","IMPRINT",EDGE,{"derivedFrom":sQuery(id+"F0.wireOp",EDGE,"E101")}),1.0]])]});
            var Q21;
            Q21=makeQuery(id+"F0.imprint","IMPRINT",FACE,{"disambiguationData":[TD([[makeQuery(id+"F0.imprint","IMPRINT",EDGE,{"derivedFrom":sQuery(id+"F0.wireOp",EDGE,"E628")}),1.0]])]});
            var Q22;
            Q22=makeQuery(id+"F0.imprint","IMPRINT",FACE,{"disambiguationData":[TD([[makeQuery(id+"F0.imprint","IMPRINT",EDGE,{"derivedFrom":sQuery(id+"F0.wireOp",EDGE,"E620")}),1.0]])]});
            var Q23;
            Q23=makeQuery(id+"F0.imprint","IMPRINT",FACE,{"disambiguationData":[TD([[makeQuery(id+"F0.imprint","IMPRINT",EDGE,{"derivedFrom":sQuery(id+"F0.wireOp",EDGE,"E439")}),-1.0]])]});
            var Q24;
            Q24=makeQuery(id+"F0.imprint","IMPRINT",FACE,{"disambiguationData":[TD([[makeQuery(id+"F0.imprint","IMPRINT",EDGE,{"derivedFrom":sQuery(id+"F0.wireOp",EDGE,"E615")}),-1.0]])]});
            var Q25;
            Q25=makeQuery(id+"F0.imprint","IMPRINT",FACE,{"disambiguationData":[TD([[makeQuery(id+"F0.imprint","IMPRINT",EDGE,{"derivedFrom":sQuery(id+"F0.wireOp",EDGE,"E620")}),-1.0]])]});
            var Q26;
            Q26=makeQuery(id+"F0.imprint","IMPRINT",FACE,{"disambiguationData":[TD([[makeQuery(id+"F0.imprint","IMPRINT",EDGE,{"derivedFrom":sQuery(id+"F0.wireOp",EDGE,"E527")}),-1.0]])]});
            var Q27;
            Q27=makeQuery(id+"F0.imprint","IMPRINT",FACE,{"disambiguationData":[TD([[makeQuery(id+"F0.imprint","IMPRINT",EDGE,{"derivedFrom":sQuery(id+"F0.wireOp",EDGE,"E821")}),-1.0]])]});
            var Q28;
            Q28=makeQuery(id+"F0.imprint","IMPRINT",FACE,{"disambiguationData":[TD([[makeQuery(id+"F0.imprint","IMPRINT",EDGE,{"derivedFrom":sQuery(id+"F0.wireOp",EDGE,"E544")}),-1.0]])]});
            var Q29;
            Q29=makeQuery(id+"F0.imprint","IMPRINT",FACE,{"disambiguationData":[TD([[makeQuery(id+"F0.imprint","IMPRINT",EDGE,{"derivedFrom":sQuery(id+"F0.wireOp",EDGE,"E245")}),-1.0]])]});
            var Q30;
            Q30=makeQuery(id+"F0.imprint","IMPRINT",FACE,{"disambiguationData":[TD([[makeQuery(id+"F0.imprint","IMPRINT",EDGE,{"derivedFrom":sQuery(id+"F0.wireOp",EDGE,"E1098")}),-1.0]])]});
            var Q31;
            Q31=makeQuery(id+"F0.imprint","IMPRINT",FACE,{"disambiguationData":[TD([[makeQuery(id+"F0.imprint","IMPRINT",EDGE,{"derivedFrom":sQuery(id+"F0.wireOp",EDGE,"E147")}),-1.0]])]});
            var Q32;
            Q32=makeQuery(id+"F0.imprint","IMPRINT",FACE,{"disambiguationData":[TD([[makeQuery(id+"F0.imprint","IMPRINT",EDGE,{"derivedFrom":sQuery(id+"F0.wireOp",EDGE,"E962")}),-1.0]])]});
            var Q33;
            Q33=makeQuery(id+"F0.imprint","IMPRINT",FACE,{"disambiguationData":[TD([[makeQuery(id+"F0.imprint","IMPRINT",EDGE,{"derivedFrom":sQuery(id+"F0.wireOp",EDGE,"E38")}),-1.0]])]});
            var Q34;
            Q34=makeQuery(id+"F0.imprint","IMPRINT",FACE,{"disambiguationData":[TD([[makeQuery(id+"F0.imprint","IMPRINT",EDGE,{"derivedFrom":sQuery(id+"F0.wireOp",EDGE,"E137")}),-1.0]])]});
            var Q35;
            Q35=makeQuery(id+"F0.imprint","IMPRINT",FACE,{"disambiguationData":[TD([[makeQuery(id+"F0.imprint","IMPRINT",EDGE,{"derivedFrom":sQuery(id+"F0.wireOp",EDGE,"E511")}),1.0]])]});
            var Q36;
            Q36=makeQuery(id+"F0.imprint","IMPRINT",FACE,{"disambiguationData":[TD([[makeQuery(id+"F0.imprint","IMPRINT",EDGE,{"derivedFrom":sQuery(id+"F0.wireOp",EDGE,"E107")}),-1.0]])]});
            var Q37;
            Q37=makeQuery(id+"F0.imprint","IMPRINT",FACE,{"disambiguationData":[TD([[makeQuery(id+"F0.imprint","IMPRINT",EDGE,{"derivedFrom":sQuery(id+"F0.wireOp",EDGE,"E167")}),-1.0]])]});
            var Q38;
            Q38=makeQuery(id+"F0.imprint","IMPRINT",FACE,{"disambiguationData":[TD([[makeQuery(id+"F0.imprint","IMPRINT",EDGE,{"derivedFrom":sQuery(id+"F0.wireOp",EDGE,"E548")}),-1.0]])]});
            var Q39;
            Q39=makeQuery(id+"F0.imprint","IMPRINT",FACE,{"disambiguationData":[TD([[makeQuery(id+"F0.imprint","IMPRINT",EDGE,{"derivedFrom":sQuery(id+"F0.wireOp",EDGE,"E65")}),-1.0]])]});
            var Q40;
            Q40=makeQuery(id+"F0.imprint","IMPRINT",FACE,{"disambiguationData":[TD([[makeQuery(id+"F0.imprint","IMPRINT",EDGE,{"derivedFrom":sQuery(id+"F0.wireOp",EDGE,"E495")}),-1.0]])]});
            var Q41;
            Q41=makeQuery(id+"F0.imprint","IMPRINT",FACE,{"disambiguationData":[TD([[makeQuery(id+"F0.imprint","IMPRINT",EDGE,{"derivedFrom":sQuery(id+"F0.wireOp",EDGE,"E83")}),-1.0]])]});
            var Q42;
            Q42=makeQuery(id+"F0.imprint","IMPRINT",FACE,{"disambiguationData":[TD([[makeQuery(id+"F0.imprint","IMPRINT",EDGE,{"derivedFrom":sQuery(id+"F0.wireOp",EDGE,"E485")}),-1.0]])]});
            var Q43;
            Q43=makeQuery(id+"F0.imprint","IMPRINT",FACE,{"disambiguationData":[TD([[makeQuery(id+"F0.imprint","IMPRINT",EDGE,{"derivedFrom":sQuery(id+"F0.wireOp",EDGE,"E92")}),-1.0]])]});
            var Q44;
            Q44=makeQuery(id+"F0.imprint","IMPRINT",FACE,{"disambiguationData":[TD([[makeQuery(id+"F0.imprint","IMPRINT",EDGE,{"derivedFrom":sQuery(id+"F0.wireOp",EDGE,"E20")}),-1.0]])]});
            var Q45;
            Q45=makeQuery(id+"F0.imprint","IMPRINT",FACE,{"disambiguationData":[TD([[makeQuery(id+"F0.imprint","IMPRINT",EDGE,{"derivedFrom":sQuery(id+"F0.wireOp",EDGE,"E15")}),-1.0]])]});
            var Q46;
            Q46=makeQuery(id+"F0.imprint","IMPRINT",FACE,{"disambiguationData":[TD([[makeQuery(id+"F0.imprint","IMPRINT",EDGE,{"derivedFrom":sQuery(id+"F0.wireOp",EDGE,"E519")}),1.0]])]});
            var Q47;
            Q47=makeQuery(id+"F0.imprint","IMPRINT",FACE,{"disambiguationData":[TD([[makeQuery(id+"F0.imprint","IMPRINT",EDGE,{"derivedFrom":sQuery(id+"F0.wireOp",EDGE,"E10")}),-1.0]])]});
            var Q48;
            Q48=makeQuery(id+"F0.imprint","IMPRINT",FACE,{"disambiguationData":[TD([[makeQuery(id+"F0.imprint","IMPRINT",EDGE,{"derivedFrom":sQuery(id+"F0.wireOp",EDGE,"E5")}),-1.0]])]});
            var Q49;
            Q49=makeQuery(id+"F0.imprint","IMPRINT",FACE,{"disambiguationData":[TD([[makeQuery(id+"F0.imprint","IMPRINT",EDGE,{"derivedFrom":sQuery(id+"F0.wireOp",EDGE,"E0")}),-1.0]])]});
            var Q50;
            Q50=makeQuery(id+"F0.imprint","IMPRINT",FACE,{"disambiguationData":[TD([[makeQuery(id+"F0.imprint","IMPRINT",EDGE,{"derivedFrom":sQuery(id+"F0.wireOp",EDGE,"E749")}),-1.0]])]});
            var Q51;
            Q51=makeQuery(id+"F0.imprint","IMPRINT",FACE,{"disambiguationData":[TD([[makeQuery(id+"F0.imprint","IMPRINT",EDGE,{"derivedFrom":sQuery(id+"F0.wireOp",EDGE,"E56")}),-1.0]])]});
            var Q52;
            Q52=makeQuery(id+"F0.imprint","IMPRINT",FACE,{"disambiguationData":[TD([[makeQuery(id+"F0.imprint","IMPRINT",EDGE,{"derivedFrom":sQuery(id+"F0.wireOp",EDGE,"E47")}),-1.0]])]});
            var Q53;
            Q53=makeQuery(id+"F0.imprint","IMPRINT",FACE,{"disambiguationData":[TD([[makeQuery(id+"F0.imprint","IMPRINT",EDGE,{"derivedFrom":sQuery(id+"F0.wireOp",EDGE,"E74")}),-1.0]])]});
            var Q54;
            Q54=makeQuery(id+"F0.imprint","IMPRINT",FACE,{"disambiguationData":[TD([[makeQuery(id+"F0.imprint","IMPRINT",EDGE,{"derivedFrom":sQuery(id+"F0.wireOp",EDGE,"E29")}),-1.0]])]});
            var Q55;
            Q55=makeQuery(id+"F0.imprint","IMPRINT",FACE,{"disambiguationData":[TD([[makeQuery(id+"F0.imprint","IMPRINT",EDGE,{"derivedFrom":sQuery(id+"F0.wireOp",EDGE,"E92")}),1.0]])]});
            var Q56;
            Q56=makeQuery(id+"F0.imprint","IMPRINT",FACE,{"disambiguationData":[TD([[makeQuery(id+"F0.imprint","IMPRINT",EDGE,{"derivedFrom":sQuery(id+"F0.wireOp",EDGE,"E74")}),1.0]])]});
            var Q57;
            Q57=makeQuery(id+"F0.imprint","IMPRINT",FACE,{"disambiguationData":[TD([[makeQuery(id+"F0.imprint","IMPRINT",EDGE,{"derivedFrom":sQuery(id+"F0.wireOp",EDGE,"E38")}),1.0]])]});
            var Q58;
            Q58=makeQuery(id+"F0.imprint","IMPRINT",FACE,{"disambiguationData":[TD([[makeQuery(id+"F0.imprint","IMPRINT",EDGE,{"derivedFrom":sQuery(id+"F0.wireOp",EDGE,"E101")}),-1.0]])]});
            var Q59;
            Q59=makeQuery(id+"F0.imprint","IMPRINT",FACE,{"disambiguationData":[TD([[makeQuery(id+"F0.imprint","IMPRINT",EDGE,{"derivedFrom":sQuery(id+"F0.wireOp",EDGE,"E480")}),1.0]])]});
            var Q60;
            Q60=makeQuery(id+"F0.imprint","IMPRINT",FACE,{"disambiguationData":[TD([[makeQuery(id+"F0.imprint","IMPRINT",EDGE,{"derivedFrom":sQuery(id+"F0.wireOp",EDGE,"E83")}),1.0]])]});
            var Q61;
            Q61=makeQuery(id+"F0.imprint","IMPRINT",FACE,{"disambiguationData":[TD([[makeQuery(id+"F0.imprint","IMPRINT",EDGE,{"derivedFrom":sQuery(id+"F0.wireOp",EDGE,"E65")}),1.0]])]});
            var Q62;
            Q62=makeQuery(id+"F0.imprint","IMPRINT",FACE,{"disambiguationData":[TD([[makeQuery(id+"F0.imprint","IMPRINT",EDGE,{"derivedFrom":sQuery(id+"F0.wireOp",EDGE,"E56")}),1.0]])]});
            var Q63;
            Q63=makeQuery(id+"F0.imprint","IMPRINT",FACE,{"disambiguationData":[TD([[makeQuery(id+"F0.imprint","IMPRINT",EDGE,{"derivedFrom":sQuery(id+"F0.wireOp",EDGE,"E20")}),1.0]])]});
            var Q64;
            Q64=makeQuery(id+"F0.imprint","IMPRINT",FACE,{"disambiguationData":[TD([[makeQuery(id+"F0.imprint","IMPRINT",EDGE,{"derivedFrom":sQuery(id+"F0.wireOp",EDGE,"E475")}),1.0]])]});
            var Q65;
            Q65=makeQuery(id+"F0.imprint","IMPRINT",FACE,{"disambiguationData":[TD([[makeQuery(id+"F0.imprint","IMPRINT",EDGE,{"derivedFrom":sQuery(id+"F0.wireOp",EDGE,"E47")}),1.0]])]});
            var Q66;
            Q66=makeQuery(id+"F0.imprint","IMPRINT",FACE,{"disambiguationData":[TD([[makeQuery(id+"F0.imprint","IMPRINT",EDGE,{"derivedFrom":sQuery(id+"F0.wireOp",EDGE,"E29")}),1.0]])]});
            var Q67;
            Q67=makeQuery(id+"F0.imprint","IMPRINT",FACE,{"disambiguationData":[TD([[makeQuery(id+"F0.imprint","IMPRINT",EDGE,{"derivedFrom":sQuery(id+"F0.wireOp",EDGE,"E15")}),1.0]])]});
            var Q68;
            Q68=makeQuery(id+"F0.imprint","IMPRINT",FACE,{"disambiguationData":[TD([[makeQuery(id+"F0.imprint","IMPRINT",EDGE,{"derivedFrom":sQuery(id+"F0.wireOp",EDGE,"E10")}),1.0]])]});
            var Q69;
            Q69=makeQuery(id+"F0.imprint","IMPRINT",FACE,{"disambiguationData":[TD([[makeQuery(id+"F0.imprint","IMPRINT",EDGE,{"derivedFrom":sQuery(id+"F0.wireOp",EDGE,"E5")}),1.0]])]});
            var Q70;
            Q70=makeQuery(id+"F0.imprint","IMPRINT",FACE,{"disambiguationData":[TD([[makeQuery(id+"F0.imprint","IMPRINT",EDGE,{"derivedFrom":sQuery(id+"F0.wireOp",EDGE,"E0")}),1.0]])]});
            var Q71;
            Q71=makeQuery(id+"F0.imprint","IMPRINT",FACE,{"disambiguationData":[TD([[makeQuery(id+"F0.imprint","IMPRINT",EDGE,{"derivedFrom":sQuery(id+"F0.wireOp",EDGE,"E628")}),-1.0]])]});
            extrude(context, id + "F1", {"entities" : qUnion([Q0, Q1, Q2, Q3, Q4, Q5, Q6, Q7, Q8, Q9, Q10, Q11, Q12, Q13, Q14, Q15, Q16, Q17, Q18, Q19, Q20, Q21, Q22, Q23, Q24, Q25, Q26, Q27, Q28, Q29, Q30, Q31, Q32, Q33, Q34, Q35, Q36, Q37, Q38, Q39, Q40, Q41, Q42, Q43, Q44, Q45, Q46, Q47, Q48, Q49, Q50, Q51, Q52, Q53, Q54, Q55, Q56, Q57, Q58, Q59, Q60, Q61, Q62, Q63, Q64, Q65, Q66, Q67, Q68, Q69, Q70, Q71]), "oppositeDirection" : true, "depth" : 1 * mm});
        }
        {
            var Q0;
            Q0=makeQuery(id+"F0.imprint","IMPRINT",FACE,{"disambiguationData":[TD([[makeQuery(id+"F0.imprint","IMPRINT",EDGE,{"derivedFrom":sQuery(id+"F0.wireOp",EDGE,"E900")}),-1.0]])]});
            var Q1;
            Q1=makeQuery(id+"F0.imprint","IMPRINT",FACE,{"disambiguationData":[TD([[makeQuery(id+"F0.imprint","IMPRINT",EDGE,{"derivedFrom":sQuery(id+"F0.wireOp",EDGE,"E821")}),-1.0]])]});
            var Q2;
            Q2=makeQuery(id+"F0.imprint","IMPRINT",FACE,{"disambiguationData":[TD([[makeQuery(id+"F0.imprint","IMPRINT",EDGE,{"derivedFrom":sQuery(id+"F0.wireOp",EDGE,"E620")}),-1.0]])]});
            var Q3;
            Q3=makeQuery(id+"F0.imprint","IMPRINT",FACE,{"disambiguationData":[TD([[makeQuery(id+"F0.imprint","IMPRINT",EDGE,{"derivedFrom":sQuery(id+"F0.wireOp",EDGE,"E962")}),-1.0]])]});
            var Q4;
            Q4=makeQuery(id+"F0.imprint","IMPRINT",FACE,{"disambiguationData":[TD([[makeQuery(id+"F0.imprint","IMPRINT",EDGE,{"derivedFrom":sQuery(id+"F0.wireOp",EDGE,"E805")}),-1.0]])]});
            var Q5;
            Q5=makeQuery(id+"F0.imprint","IMPRINT",FACE,{"disambiguationData":[TD([[makeQuery(id+"F0.imprint","IMPRINT",EDGE,{"derivedFrom":sQuery(id+"F0.wireOp",EDGE,"E787")}),-1.0]])]});
            var Q6;
            Q6=makeQuery(id+"F0.imprint","IMPRINT",FACE,{"disambiguationData":[TD([[makeQuery(id+"F0.imprint","IMPRINT",EDGE,{"derivedFrom":sQuery(id+"F0.wireOp",EDGE,"E594")}),-1.0]])]});
            var Q7;
            Q7=makeQuery(id+"F0.imprint","IMPRINT",FACE,{"disambiguationData":[TD([[makeQuery(id+"F0.imprint","IMPRINT",EDGE,{"derivedFrom":sQuery(id+"F0.wireOp",EDGE,"E559")}),-1.0]])]});
            var Q8;
            Q8=makeQuery(id+"F0.imprint","IMPRINT",FACE,{"disambiguationData":[TD([[makeQuery(id+"F0.imprint","IMPRINT",EDGE,{"derivedFrom":sQuery(id+"F0.wireOp",EDGE,"E610")}),-1.0]])]});
            var Q9;
            Q9=makeQuery(id+"F0.imprint","IMPRINT",FACE,{"disambiguationData":[TD([[makeQuery(id+"F0.imprint","IMPRINT",EDGE,{"derivedFrom":sQuery(id+"F0.wireOp",EDGE,"E590")}),-1.0]])]});
            var Q10;
            Q10=makeQuery(id+"F0.imprint","IMPRINT",FACE,{"disambiguationData":[TD([[makeQuery(id+"F0.imprint","IMPRINT",EDGE,{"derivedFrom":sQuery(id+"F0.wireOp",EDGE,"E615")}),-1.0]])]});
            var Q11;
            Q11=makeQuery(id+"F0.imprint","IMPRINT",FACE,{"disambiguationData":[TD([[makeQuery(id+"F0.imprint","IMPRINT",EDGE,{"derivedFrom":sQuery(id+"F0.wireOp",EDGE,"E628")}),1.0]])]});
            var Q12;
            Q12=makeQuery(id+"F0.imprint","IMPRINT",FACE,{"disambiguationData":[TD([[makeQuery(id+"F0.imprint","IMPRINT",EDGE,{"derivedFrom":sQuery(id+"F0.wireOp",EDGE,"E1098")}),-1.0]])]});
            var Q13;
            Q13=makeQuery(id+"F0.imprint","IMPRINT",FACE,{"disambiguationData":[TD([[makeQuery(id+"F0.imprint","IMPRINT",EDGE,{"derivedFrom":sQuery(id+"F0.wireOp",EDGE,"E711")}),1.0]])]});
            var Q14;
            Q14=makeQuery(id+"F0.imprint","IMPRINT",FACE,{"disambiguationData":[TD([[makeQuery(id+"F0.imprint","IMPRINT",EDGE,{"derivedFrom":sQuery(id+"F0.wireOp",EDGE,"E167")}),-1.0]])]});
            var Q15;
            Q15=makeQuery(id+"F0.imprint","IMPRINT",FACE,{"disambiguationData":[TD([[makeQuery(id+"F0.imprint","IMPRINT",EDGE,{"derivedFrom":sQuery(id+"F0.wireOp",EDGE,"E495")}),-1.0]])]});
            var Q16;
            Q16=makeQuery(id+"F0.imprint","IMPRINT",FACE,{"disambiguationData":[TD([[makeQuery(id+"F0.imprint","IMPRINT",EDGE,{"derivedFrom":sQuery(id+"F0.wireOp",EDGE,"E92")}),-1.0]])]});
            var Q17;
            Q17=makeQuery(id+"F0.imprint","IMPRINT",FACE,{"disambiguationData":[TD([[makeQuery(id+"F0.imprint","IMPRINT",EDGE,{"derivedFrom":sQuery(id+"F0.wireOp",EDGE,"E439")}),-1.0]])]});
            var Q18;
            Q18=makeQuery(id+"F0.imprint","IMPRINT",FACE,{"disambiguationData":[TD([[makeQuery(id+"F0.imprint","IMPRINT",EDGE,{"derivedFrom":sQuery(id+"F0.wireOp",EDGE,"E83")}),-1.0]])]});
            var Q19;
            Q19=makeQuery(id+"F0.imprint","IMPRINT",FACE,{"disambiguationData":[TD([[makeQuery(id+"F0.imprint","IMPRINT",EDGE,{"derivedFrom":sQuery(id+"F0.wireOp",EDGE,"E407")}),-1.0]])]});
            var Q20;
            Q20=makeQuery(id+"F0.imprint","IMPRINT",FACE,{"disambiguationData":[TD([[makeQuery(id+"F0.imprint","IMPRINT",EDGE,{"derivedFrom":sQuery(id+"F0.wireOp",EDGE,"E65")}),-1.0]])]});
            var Q21;
            Q21=makeQuery(id+"F0.imprint","IMPRINT",FACE,{"disambiguationData":[TD([[makeQuery(id+"F0.imprint","IMPRINT",EDGE,{"derivedFrom":sQuery(id+"F0.wireOp",EDGE,"E15")}),-1.0]])]});
            var Q22;
            Q22=makeQuery(id+"F0.imprint","IMPRINT",FACE,{"disambiguationData":[TD([[makeQuery(id+"F0.imprint","IMPRINT",EDGE,{"derivedFrom":sQuery(id+"F0.wireOp",EDGE,"E157")}),-1.0]])]});
            var Q23;
            Q23=makeQuery(id+"F0.imprint","IMPRINT",FACE,{"disambiguationData":[TD([[makeQuery(id+"F0.imprint","IMPRINT",EDGE,{"derivedFrom":sQuery(id+"F0.wireOp",EDGE,"E10")}),-1.0]])]});
            var Q24;
            Q24=makeQuery(id+"F0.imprint","IMPRINT",FACE,{"disambiguationData":[TD([[makeQuery(id+"F0.imprint","IMPRINT",EDGE,{"derivedFrom":sQuery(id+"F0.wireOp",EDGE,"E548")}),-1.0]])]});
            var Q25;
            Q25=makeQuery(id+"F0.imprint","IMPRINT",FACE,{"disambiguationData":[TD([[makeQuery(id+"F0.imprint","IMPRINT",EDGE,{"derivedFrom":sQuery(id+"F0.wireOp",EDGE,"E5")}),-1.0]])]});
            var Q26;
            Q26=makeQuery(id+"F0.imprint","IMPRINT",FACE,{"disambiguationData":[TD([[makeQuery(id+"F0.imprint","IMPRINT",EDGE,{"derivedFrom":sQuery(id+"F0.wireOp",EDGE,"E544")}),-1.0]])]});
            var Q27;
            Q27=makeQuery(id+"F0.imprint","IMPRINT",FACE,{"disambiguationData":[TD([[makeQuery(id+"F0.imprint","IMPRINT",EDGE,{"derivedFrom":sQuery(id+"F0.wireOp",EDGE,"E74")}),-1.0]])]});
            var Q28;
            Q28=makeQuery(id+"F0.imprint","IMPRINT",FACE,{"disambiguationData":[TD([[makeQuery(id+"F0.imprint","IMPRINT",EDGE,{"derivedFrom":sQuery(id+"F0.wireOp",EDGE,"E56")}),-1.0]])]});
            var Q29;
            Q29=makeQuery(id+"F0.imprint","IMPRINT",FACE,{"disambiguationData":[TD([[makeQuery(id+"F0.imprint","IMPRINT",EDGE,{"derivedFrom":sQuery(id+"F0.wireOp",EDGE,"E291")}),-1.0]])]});
            var Q30;
            Q30=makeQuery(id+"F0.imprint","IMPRINT",FACE,{"disambiguationData":[TD([[makeQuery(id+"F0.imprint","IMPRINT",EDGE,{"derivedFrom":sQuery(id+"F0.wireOp",EDGE,"E0")}),-1.0]])]});
            var Q31;
            Q31=makeQuery(id+"F0.imprint","IMPRINT",FACE,{"disambiguationData":[TD([[makeQuery(id+"F0.imprint","IMPRINT",EDGE,{"derivedFrom":sQuery(id+"F0.wireOp",EDGE,"E257")}),-1.0]])]});
            var Q32;
            Q32=makeQuery(id+"F0.imprint","IMPRINT",FACE,{"disambiguationData":[TD([[makeQuery(id+"F0.imprint","IMPRINT",EDGE,{"derivedFrom":sQuery(id+"F0.wireOp",EDGE,"E245")}),-1.0]])]});
            var Q33;
            Q33=makeQuery(id+"F0.imprint","IMPRINT",FACE,{"disambiguationData":[TD([[makeQuery(id+"F0.imprint","IMPRINT",EDGE,{"derivedFrom":sQuery(id+"F0.wireOp",EDGE,"E47")}),-1.0]])]});
            var Q34;
            Q34=makeQuery(id+"F0.imprint","IMPRINT",FACE,{"disambiguationData":[TD([[makeQuery(id+"F0.imprint","IMPRINT",EDGE,{"derivedFrom":sQuery(id+"F0.wireOp",EDGE,"E217")}),-1.0]])]});
            var Q35;
            Q35=makeQuery(id+"F0.imprint","IMPRINT",FACE,{"disambiguationData":[TD([[makeQuery(id+"F0.imprint","IMPRINT",EDGE,{"derivedFrom":sQuery(id+"F0.wireOp",EDGE,"E38")}),-1.0]])]});
            var Q36;
            Q36=makeQuery(id+"F0.imprint","IMPRINT",FACE,{"disambiguationData":[TD([[makeQuery(id+"F0.imprint","IMPRINT",EDGE,{"derivedFrom":sQuery(id+"F0.wireOp",EDGE,"E107")}),-1.0]])]});
            var Q37;
            Q37=makeQuery(id+"F0.imprint","IMPRINT",FACE,{"disambiguationData":[TD([[makeQuery(id+"F0.imprint","IMPRINT",EDGE,{"derivedFrom":sQuery(id+"F0.wireOp",EDGE,"E147")}),-1.0]])]});
            var Q38;
            Q38=makeQuery(id+"F0.imprint","IMPRINT",FACE,{"disambiguationData":[TD([[makeQuery(id+"F0.imprint","IMPRINT",EDGE,{"derivedFrom":sQuery(id+"F0.wireOp",EDGE,"E137")}),-1.0]])]});
            var Q39;
            Q39=makeQuery(id+"F0.imprint","IMPRINT",FACE,{"disambiguationData":[TD([[makeQuery(id+"F0.imprint","IMPRINT",EDGE,{"derivedFrom":sQuery(id+"F0.wireOp",EDGE,"E485")}),-1.0]])]});
            var Q40;
            Q40=makeQuery(id+"F0.imprint","IMPRINT",FACE,{"disambiguationData":[TD([[makeQuery(id+"F0.imprint","IMPRINT",EDGE,{"derivedFrom":sQuery(id+"F0.wireOp",EDGE,"E527")}),-1.0]])]});
            var Q41;
            Q41=makeQuery(id+"F0.imprint","IMPRINT",FACE,{"disambiguationData":[TD([[makeQuery(id+"F0.imprint","IMPRINT",EDGE,{"derivedFrom":sQuery(id+"F0.wireOp",EDGE,"E101")}),-1.0]])]});
            var Q42;
            Q42=makeQuery(id+"F0.imprint","IMPRINT",FACE,{"disambiguationData":[TD([[makeQuery(id+"F0.imprint","IMPRINT",EDGE,{"derivedFrom":sQuery(id+"F0.wireOp",EDGE,"E202")}),-1.0]])]});
            var Q43;
            Q43=makeQuery(id+"F0.imprint","IMPRINT",FACE,{"disambiguationData":[TD([[makeQuery(id+"F0.imprint","IMPRINT",EDGE,{"derivedFrom":sQuery(id+"F0.wireOp",EDGE,"E190")}),-1.0]])]});
            var Q44;
            Q44=makeQuery(id+"F0.imprint","IMPRINT",FACE,{"disambiguationData":[TD([[makeQuery(id+"F0.imprint","IMPRINT",EDGE,{"derivedFrom":sQuery(id+"F0.wireOp",EDGE,"E505")}),-1.0]])]});
            var Q45;
            Q45=makeQuery(id+"F0.imprint","IMPRINT",FACE,{"disambiguationData":[TD([[makeQuery(id+"F0.imprint","IMPRINT",EDGE,{"derivedFrom":sQuery(id+"F0.wireOp",EDGE,"E29")}),-1.0]])]});
            var Q46;
            Q46=makeQuery(id+"F0.imprint","IMPRINT",FACE,{"disambiguationData":[TD([[makeQuery(id+"F0.imprint","IMPRINT",EDGE,{"derivedFrom":sQuery(id+"F0.wireOp",EDGE,"E20")}),-1.0]])]});
            extrude(context, id + "F2", {"entities" : qUnion([Q0, Q1, Q2, Q3, Q4, Q5, Q6, Q7, Q8, Q9, Q10, Q11, Q12, Q13, Q14, Q15, Q16, Q17, Q18, Q19, Q20, Q21, Q22, Q23, Q24, Q25, Q26, Q27, Q28, Q29, Q30, Q31, Q32, Q33, Q34, Q35, Q36, Q37, Q38, Q39, Q40, Q41, Q42, Q43, Q44, Q45, Q46]), "operationType" : NewBodyOperationType.ADD, "depth" : 1 * mm});
        }
        {
            var Q0;
            Q0=makeQuery(id+"F0.imprint","IMPRINT",FACE,{"disambiguationData":[TD([[makeQuery(id+"F0.imprint","IMPRINT",EDGE,{"derivedFrom":sQuery(id+"F0.wireOp",EDGE,"E628")}),-1.0]])]});
            var Q1;
            Q1=makeQuery(id+"F0.imprint","IMPRINT",FACE,{"disambiguationData":[TD([[makeQuery(id+"F0.imprint","IMPRINT",EDGE,{"derivedFrom":sQuery(id+"F0.wireOp",EDGE,"E699")}),-1.0]])]});
            extrude(context, id + "F3", {"entities" : qUnion([Q0, Q1]), "operationType" : NewBodyOperationType.ADD, "depth" : .5 * mm});
        }
        {
            var Q0;
            Q0=makeQuery(id+"F1.opExtrude","SWEPT_BODY",BODY,{"disambiguationData":[OSD([sQuery(id+"F0.wireOp",EDGE,"E1122.bottom"),sQuery(id+"F0.wireOp",EDGE,"E1122.top"),sQuery(id+"F0.wireOp",EDGE,"E1122.left"),sQuery(id+"F0.wireOp",EDGE,"E1122.right")])]});
            var Q1;
            Q1=qCreatedBy(makeId("Origin.pointOp"),VERTEX);
            transform(context, id + "F4", {"entities" : qUnion([Q0]), "transformType" : TransformType.SCALE_UNIFORMLY, "scale" : 6, "scalePoint" : qUnion([Q1]), "makeCopy" : false});
        }
        {
            var Q0;
            Q0=makeQuery(id+"F1.opExtrude","CAP_FACE",FACE,{"disambiguationData":[OSD([sQuery(id+"F0.wireOp",EDGE,"E1122.bottom"),sQuery(id+"F0.wireOp",EDGE,"E1122.top"),sQuery(id+"F0.wireOp",EDGE,"E1122.left"),sQuery(id+"F0.wireOp",EDGE,"E1122.right")])],"isStart":false});
            var sketch = newSketch(context, id + "F5", { "sketchPlane" : qUnion([Q0])});
            skLineSegment(sketch, "E1128.0", {"start": v(-36.35, 15.48) * mm, "end": v(36.05, 15.48) * mm});
            skLineSegment(sketch, "E1128.1", {"start": v(-36.35, -15.31) * mm, "end": v(-36.35, 15.48) * mm});
            skLineSegment(sketch, "E1128.2", {"start": v(-36.35, -15.31) * mm, "end": v(36.05, -15.31) * mm});
            skLineSegment(sketch, "E1128.3", {"start": v(36.05, -15.31) * mm, "end": v(36.05, 15.48) * mm});
            skSolve(sketch);
        }
        {
            var Q0;
            Q0=makeQuery(id+"F5.imprint","IMPRINT",FACE,{"disambiguationData":[TD([[makeQuery(id+"F5.imprint","IMPRINT",EDGE,{"derivedFrom":sQuery(id+"F5.wireOp",EDGE,"E1128.0")}),-1.0]])]});
            extrude(context, id + "F6", {"entities" : qUnion([Q0]), "operationType" : NewBodyOperationType.ADD, "oppositeDirection" : true, "depth" : 13 * mm});
        }
    });
